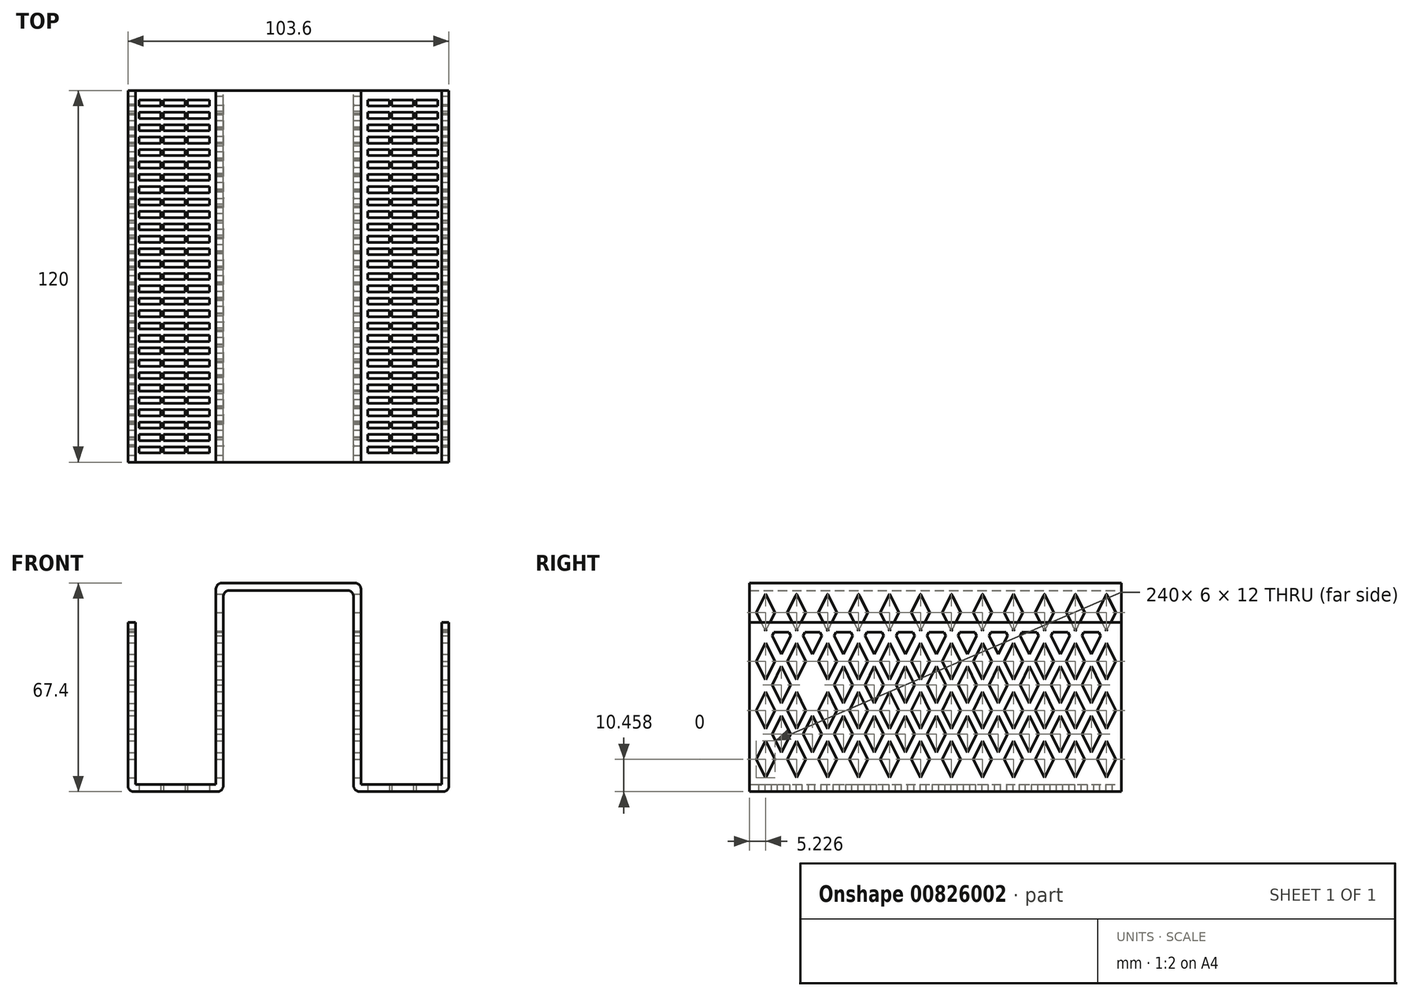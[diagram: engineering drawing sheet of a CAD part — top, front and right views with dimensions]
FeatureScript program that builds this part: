
annotation { "Feature Type Name" : "Feature", "Feature Type Description" : "" }
export const myFeature = defineFeature(function(context is Context, id is Id, definition is map)
    precondition{}
    {
        {
            var Q0;
            Q0=qCreatedBy(makeId("Front.planeOp"),FACE);
            var sketch = newSketch(context, id + "F0", { "sketchPlane" : qUnion([Q0])});
            skLineSegment(sketch, "E0", {"start": v(0, 0) * mm, "end": v(0, 123.96) * mm, "construction": true});
            skLineSegment(sketch, "E1", {"start": v(0, 43.65) * mm, "end": v(-23.4, 43.65) * mm});
            skLineSegment(sketch, "E2", {"start": v(-23.4, 43.65) * mm, "end": v(-23.4, -21.35) * mm});
            skLineSegment(sketch, "E3", {"start": v(-23.4, -21.35) * mm, "end": v(-49.4, -21.35) * mm});
            skLineSegment(sketch, "E4", {"start": v(-49.4, -21.35) * mm, "end": v(-49.4, 28.65) * mm});
            skLineSegment(sketch, "E5.MirrorCS", {"start": v(0, 43.65) * mm, "end": v(23.4, 43.65) * mm});
            skLineSegment(sketch, "E6.MirrorCS", {"start": v(23.4, 43.65) * mm, "end": v(23.4, -21.35) * mm});
            skLineSegment(sketch, "E7.MirrorCS", {"start": v(23.4, -21.35) * mm, "end": v(49.4, -21.35) * mm});
            skLineSegment(sketch, "E8.MirrorCS", {"start": v(49.4, -21.35) * mm, "end": v(49.4, 28.65) * mm});
            skLineSegment(sketch, "E9.0", {"start": v(-51.8, -23.75) * mm, "end": v(-51.8, 28.65) * mm});
            skLineSegment(sketch, "E9.1", {"start": v(-21, -23.75) * mm, "end": v(-51.8, -23.75) * mm});
            skLineSegment(sketch, "E9.2", {"start": v(-21, 41.25) * mm, "end": v(-21, -23.75) * mm});
            skLineSegment(sketch, "E9.3", {"start": v(0, 41.25) * mm, "end": v(-21, 41.25) * mm});
            skLineSegment(sketch, "E9.4", {"start": v(51.8, -23.75) * mm, "end": v(51.8, 28.65) * mm});
            skLineSegment(sketch, "E9.5", {"start": v(21, -23.75) * mm, "end": v(51.8, -23.75) * mm});
            skLineSegment(sketch, "E9.6", {"start": v(21, 41.25) * mm, "end": v(21, -23.75) * mm});
            skLineSegment(sketch, "E9.7", {"start": v(0, 41.25) * mm, "end": v(21, 41.25) * mm});
            skLineSegment(sketch, "E10", {"start": v(-51.8, 28.65) * mm, "end": v(-49.4, 28.65) * mm});
            skLineSegment(sketch, "E11", {"start": v(51.8, 28.65) * mm, "end": v(49.4, 28.65) * mm});
            skSolve(sketch);
        }
        {
            var Q0;
            Q0=makeQuery(id+"F0.imprint","IMPRINT",FACE,{"disambiguationData":[TD([[makeQuery(id+"F0.imprint","IMPRINT",EDGE,{"derivedFrom":sQuery(id+"F0.wireOp",EDGE,"E1")}),1.0]])]});
            extrude(context, id + "F1", {"entities" : qUnion([Q0]), "depth" : 60 * mm, "offsetDistance" : 25 * mm, "hasSecondDirection" : true, "secondDirectionOppositeDirection" : true, "secondDirectionDepth" : 60 * mm});
        }
        {
            var Q0;
            Q0=makeQuery(id+"F1.opExtrude","SWEPT_FACE",FACE,{"disambiguationData":[OSD([sQuery(id+"F0.wireOp",EDGE,"E9.4")])]});
            var sketch = newSketch(context, id + "F2", { "sketchPlane" : qUnion([Q0])});
            skLineSegment(sketch, "E12", {"start": v(-54.77, 34.1) * mm, "end": v(-54.77, 40.1) * mm, "construction": true});
            skLineSegment(sketch, "E13", {"start": v(-54.77, 34.1) * mm, "end": v(-54.77, 28.1) * mm, "construction": true});
            skLineSegment(sketch, "E14", {"start": v(-54.77, 34.1) * mm, "end": v(-51.77, 34.1) * mm, "construction": true});
            skLineSegment(sketch, "E15", {"start": v(-54.77, 34.1) * mm, "end": v(-57.77, 34.1) * mm, "construction": true});
            skLineSegment(sketch, "E16", {"start": v(-54.77, 40.1) * mm, "end": v(-51.77, 34.1) * mm});
            skLineSegment(sketch, "E17", {"start": v(-54.77, 28.1) * mm, "end": v(-51.77, 34.1) * mm});
            skLineSegment(sketch, "E18", {"start": v(-54.77, 28.1) * mm, "end": v(-57.77, 34.1) * mm});
            skLineSegment(sketch, "E19", {"start": v(-57.77, 34.1) * mm, "end": v(-54.77, 40.1) * mm});
            skLineSegment(sketch, "E20.0.1.0", {"start": v(-54.77, 24.3) * mm, "end": v(-51.77, 18.3) * mm});
            skLineSegment(sketch, "E20.0.1.1", {"start": v(-57.77, 18.3) * mm, "end": v(-54.77, 24.3) * mm});
            skLineSegment(sketch, "E20.0.1.2", {"start": v(-54.77, 12.3) * mm, "end": v(-57.77, 18.3) * mm});
            skLineSegment(sketch, "E20.0.1.3", {"start": v(-54.77, 12.3) * mm, "end": v(-51.77, 18.3) * mm});
            skLineSegment(sketch, "E20.0.2.0", {"start": v(-54.77, 8.5) * mm, "end": v(-51.77, 2.5) * mm});
            skLineSegment(sketch, "E20.0.2.1", {"start": v(-57.77, 2.5) * mm, "end": v(-54.77, 8.5) * mm});
            skLineSegment(sketch, "E20.0.2.2", {"start": v(-54.77, -3.5) * mm, "end": v(-57.77, 2.5) * mm});
            skLineSegment(sketch, "E20.0.2.3", {"start": v(-54.77, -3.5) * mm, "end": v(-51.77, 2.5) * mm});
            skLineSegment(sketch, "E20.0.3.0", {"start": v(-54.77, -7.3) * mm, "end": v(-51.77, -13.3) * mm});
            skLineSegment(sketch, "E20.0.3.1", {"start": v(-57.77, -13.3) * mm, "end": v(-54.77, -7.3) * mm});
            skLineSegment(sketch, "E20.0.3.2", {"start": v(-54.77, -19.3) * mm, "end": v(-57.77, -13.3) * mm});
            skLineSegment(sketch, "E20.0.3.3", {"start": v(-54.77, -19.3) * mm, "end": v(-51.77, -13.3) * mm});
            skLineSegment(sketch, "E20.1.0.0", {"start": v(-44.77, 40.1) * mm, "end": v(-41.77, 34.1) * mm});
            skLineSegment(sketch, "E20.1.0.1", {"start": v(-47.77, 34.1) * mm, "end": v(-44.77, 40.1) * mm});
            skLineSegment(sketch, "E20.1.0.2", {"start": v(-44.77, 28.1) * mm, "end": v(-47.77, 34.1) * mm});
            skLineSegment(sketch, "E20.1.0.3", {"start": v(-44.77, 28.1) * mm, "end": v(-41.77, 34.1) * mm});
            skLineSegment(sketch, "E20.1.1.0", {"start": v(-44.77, 24.3) * mm, "end": v(-41.77, 18.3) * mm});
            skLineSegment(sketch, "E20.1.1.1", {"start": v(-47.77, 18.3) * mm, "end": v(-44.77, 24.3) * mm});
            skLineSegment(sketch, "E20.1.1.2", {"start": v(-44.77, 12.3) * mm, "end": v(-47.77, 18.3) * mm});
            skLineSegment(sketch, "E20.1.1.3", {"start": v(-44.77, 12.3) * mm, "end": v(-41.77, 18.3) * mm});
            skLineSegment(sketch, "E20.1.2.0", {"start": v(-44.77, 8.5) * mm, "end": v(-41.77, 2.5) * mm});
            skLineSegment(sketch, "E20.1.2.1", {"start": v(-47.77, 2.5) * mm, "end": v(-44.77, 8.5) * mm});
            skLineSegment(sketch, "E20.1.2.2", {"start": v(-44.77, -3.5) * mm, "end": v(-47.77, 2.5) * mm});
            skLineSegment(sketch, "E20.1.2.3", {"start": v(-44.77, -3.5) * mm, "end": v(-41.77, 2.5) * mm});
            skLineSegment(sketch, "E20.1.3.0", {"start": v(-44.77, -7.3) * mm, "end": v(-41.77, -13.3) * mm});
            skLineSegment(sketch, "E20.1.3.1", {"start": v(-47.77, -13.3) * mm, "end": v(-44.77, -7.3) * mm});
            skLineSegment(sketch, "E20.1.3.2", {"start": v(-44.77, -19.3) * mm, "end": v(-47.77, -13.3) * mm});
            skLineSegment(sketch, "E20.1.3.3", {"start": v(-44.77, -19.3) * mm, "end": v(-41.77, -13.3) * mm});
            skLineSegment(sketch, "E20.2.0.0", {"start": v(-34.77, 40.1) * mm, "end": v(-31.77, 34.1) * mm});
            skLineSegment(sketch, "E20.2.0.1", {"start": v(-37.77, 34.1) * mm, "end": v(-34.77, 40.1) * mm});
            skLineSegment(sketch, "E20.2.0.2", {"start": v(-34.77, 28.1) * mm, "end": v(-37.77, 34.1) * mm});
            skLineSegment(sketch, "E20.2.0.3", {"start": v(-34.77, 28.1) * mm, "end": v(-31.77, 34.1) * mm});
            skLineSegment(sketch, "E20.2.1.0", {"start": v(-34.77, 24.3) * mm, "end": v(-31.77, 18.3) * mm});
            skLineSegment(sketch, "E20.2.1.1", {"start": v(-37.77, 18.3) * mm, "end": v(-34.77, 24.3) * mm});
            skLineSegment(sketch, "E20.2.1.2", {"start": v(-34.77, 12.3) * mm, "end": v(-37.77, 18.3) * mm});
            skLineSegment(sketch, "E20.2.1.3", {"start": v(-34.77, 12.3) * mm, "end": v(-31.77, 18.3) * mm});
            skLineSegment(sketch, "E20.2.2.0", {"start": v(-34.77, 8.5) * mm, "end": v(-31.77, 2.5) * mm});
            skLineSegment(sketch, "E20.2.2.1", {"start": v(-37.77, 2.5) * mm, "end": v(-34.77, 8.5) * mm});
            skLineSegment(sketch, "E20.2.2.2", {"start": v(-34.77, -3.5) * mm, "end": v(-37.77, 2.5) * mm});
            skLineSegment(sketch, "E20.2.2.3", {"start": v(-34.77, -3.5) * mm, "end": v(-31.77, 2.5) * mm});
            skLineSegment(sketch, "E20.2.3.0", {"start": v(-34.77, -7.3) * mm, "end": v(-31.77, -13.3) * mm});
            skLineSegment(sketch, "E20.2.3.1", {"start": v(-37.77, -13.3) * mm, "end": v(-34.77, -7.3) * mm});
            skLineSegment(sketch, "E20.2.3.2", {"start": v(-34.77, -19.3) * mm, "end": v(-37.77, -13.3) * mm});
            skLineSegment(sketch, "E20.2.3.3", {"start": v(-34.77, -19.3) * mm, "end": v(-31.77, -13.3) * mm});
            skLineSegment(sketch, "E20.3.0.0", {"start": v(-24.77, 40.1) * mm, "end": v(-21.77, 34.1) * mm});
            skLineSegment(sketch, "E20.3.0.1", {"start": v(-27.77, 34.1) * mm, "end": v(-24.77, 40.1) * mm});
            skLineSegment(sketch, "E20.3.0.2", {"start": v(-24.77, 28.1) * mm, "end": v(-27.77, 34.1) * mm});
            skLineSegment(sketch, "E20.3.0.3", {"start": v(-24.77, 28.1) * mm, "end": v(-21.77, 34.1) * mm});
            skLineSegment(sketch, "E20.3.1.0", {"start": v(-24.77, 24.3) * mm, "end": v(-21.77, 18.3) * mm});
            skLineSegment(sketch, "E20.3.1.1", {"start": v(-27.77, 18.3) * mm, "end": v(-24.77, 24.3) * mm});
            skLineSegment(sketch, "E20.3.1.2", {"start": v(-24.77, 12.3) * mm, "end": v(-27.77, 18.3) * mm});
            skLineSegment(sketch, "E20.3.1.3", {"start": v(-24.77, 12.3) * mm, "end": v(-21.77, 18.3) * mm});
            skLineSegment(sketch, "E20.3.2.0", {"start": v(-24.77, 8.5) * mm, "end": v(-21.77, 2.5) * mm});
            skLineSegment(sketch, "E20.3.2.1", {"start": v(-27.77, 2.5) * mm, "end": v(-24.77, 8.5) * mm});
            skLineSegment(sketch, "E20.3.2.2", {"start": v(-24.77, -3.5) * mm, "end": v(-27.77, 2.5) * mm});
            skLineSegment(sketch, "E20.3.2.3", {"start": v(-24.77, -3.5) * mm, "end": v(-21.77, 2.5) * mm});
            skLineSegment(sketch, "E20.3.3.0", {"start": v(-24.77, -7.3) * mm, "end": v(-21.77, -13.3) * mm});
            skLineSegment(sketch, "E20.3.3.1", {"start": v(-27.77, -13.3) * mm, "end": v(-24.77, -7.3) * mm});
            skLineSegment(sketch, "E20.3.3.2", {"start": v(-24.77, -19.3) * mm, "end": v(-27.77, -13.3) * mm});
            skLineSegment(sketch, "E20.3.3.3", {"start": v(-24.77, -19.3) * mm, "end": v(-21.77, -13.3) * mm});
            skLineSegment(sketch, "E20.4.0.0", {"start": v(-14.77, 40.1) * mm, "end": v(-11.77, 34.1) * mm});
            skLineSegment(sketch, "E20.4.0.1", {"start": v(-17.77, 34.1) * mm, "end": v(-14.77, 40.1) * mm});
            skLineSegment(sketch, "E20.4.0.2", {"start": v(-14.77, 28.1) * mm, "end": v(-17.77, 34.1) * mm});
            skLineSegment(sketch, "E20.4.0.3", {"start": v(-14.77, 28.1) * mm, "end": v(-11.77, 34.1) * mm});
            skLineSegment(sketch, "E20.4.1.0", {"start": v(-14.77, 24.3) * mm, "end": v(-11.77, 18.3) * mm});
            skLineSegment(sketch, "E20.4.1.1", {"start": v(-17.77, 18.3) * mm, "end": v(-14.77, 24.3) * mm});
            skLineSegment(sketch, "E20.4.1.2", {"start": v(-14.77, 12.3) * mm, "end": v(-17.77, 18.3) * mm});
            skLineSegment(sketch, "E20.4.1.3", {"start": v(-14.77, 12.3) * mm, "end": v(-11.77, 18.3) * mm});
            skLineSegment(sketch, "E20.4.2.0", {"start": v(-14.77, 8.5) * mm, "end": v(-11.77, 2.5) * mm});
            skLineSegment(sketch, "E20.4.2.1", {"start": v(-17.77, 2.5) * mm, "end": v(-14.77, 8.5) * mm});
            skLineSegment(sketch, "E20.4.2.2", {"start": v(-14.77, -3.5) * mm, "end": v(-17.77, 2.5) * mm});
            skLineSegment(sketch, "E20.4.2.3", {"start": v(-14.77, -3.5) * mm, "end": v(-11.77, 2.5) * mm});
            skLineSegment(sketch, "E20.4.3.0", {"start": v(-14.77, -7.3) * mm, "end": v(-11.77, -13.3) * mm});
            skLineSegment(sketch, "E20.4.3.1", {"start": v(-17.77, -13.3) * mm, "end": v(-14.77, -7.3) * mm});
            skLineSegment(sketch, "E20.4.3.2", {"start": v(-14.77, -19.3) * mm, "end": v(-17.77, -13.3) * mm});
            skLineSegment(sketch, "E20.4.3.3", {"start": v(-14.77, -19.3) * mm, "end": v(-11.77, -13.3) * mm});
            skLineSegment(sketch, "E20.5.0.0", {"start": v(-4.77, 40.1) * mm, "end": v(-1.77, 34.1) * mm});
            skLineSegment(sketch, "E20.5.0.1", {"start": v(-7.77, 34.1) * mm, "end": v(-4.77, 40.1) * mm});
            skLineSegment(sketch, "E20.5.0.2", {"start": v(-4.77, 28.1) * mm, "end": v(-7.77, 34.1) * mm});
            skLineSegment(sketch, "E20.5.0.3", {"start": v(-4.77, 28.1) * mm, "end": v(-1.77, 34.1) * mm});
            skLineSegment(sketch, "E20.5.1.0", {"start": v(-4.77, 24.3) * mm, "end": v(-1.77, 18.3) * mm});
            skLineSegment(sketch, "E20.5.1.1", {"start": v(-7.77, 18.3) * mm, "end": v(-4.77, 24.3) * mm});
            skLineSegment(sketch, "E20.5.1.2", {"start": v(-4.77, 12.3) * mm, "end": v(-7.77, 18.3) * mm});
            skLineSegment(sketch, "E20.5.1.3", {"start": v(-4.77, 12.3) * mm, "end": v(-1.77, 18.3) * mm});
            skLineSegment(sketch, "E20.5.2.0", {"start": v(-4.77, 8.5) * mm, "end": v(-1.77, 2.5) * mm});
            skLineSegment(sketch, "E20.5.2.1", {"start": v(-7.77, 2.5) * mm, "end": v(-4.77, 8.5) * mm});
            skLineSegment(sketch, "E20.5.2.2", {"start": v(-4.77, -3.5) * mm, "end": v(-7.77, 2.5) * mm});
            skLineSegment(sketch, "E20.5.2.3", {"start": v(-4.77, -3.5) * mm, "end": v(-1.77, 2.5) * mm});
            skLineSegment(sketch, "E20.5.3.0", {"start": v(-4.77, -7.3) * mm, "end": v(-1.77, -13.3) * mm});
            skLineSegment(sketch, "E20.5.3.1", {"start": v(-7.77, -13.3) * mm, "end": v(-4.77, -7.3) * mm});
            skLineSegment(sketch, "E20.5.3.2", {"start": v(-4.77, -19.3) * mm, "end": v(-7.77, -13.3) * mm});
            skLineSegment(sketch, "E20.5.3.3", {"start": v(-4.77, -19.3) * mm, "end": v(-1.77, -13.3) * mm});
            skLineSegment(sketch, "E20.6.0.0", {"start": v(5.23, 40.1) * mm, "end": v(8.23, 34.1) * mm});
            skLineSegment(sketch, "E20.6.0.1", {"start": v(2.23, 34.1) * mm, "end": v(5.23, 40.1) * mm});
            skLineSegment(sketch, "E20.6.0.2", {"start": v(5.23, 28.1) * mm, "end": v(2.23, 34.1) * mm});
            skLineSegment(sketch, "E20.6.0.3", {"start": v(5.23, 28.1) * mm, "end": v(8.23, 34.1) * mm});
            skLineSegment(sketch, "E20.6.1.0", {"start": v(5.23, 24.3) * mm, "end": v(8.23, 18.3) * mm});
            skLineSegment(sketch, "E20.6.1.1", {"start": v(2.23, 18.3) * mm, "end": v(5.23, 24.3) * mm});
            skLineSegment(sketch, "E20.6.1.2", {"start": v(5.23, 12.3) * mm, "end": v(2.23, 18.3) * mm});
            skLineSegment(sketch, "E20.6.1.3", {"start": v(5.23, 12.3) * mm, "end": v(8.23, 18.3) * mm});
            skLineSegment(sketch, "E20.6.2.0", {"start": v(5.23, 8.5) * mm, "end": v(8.23, 2.5) * mm});
            skLineSegment(sketch, "E20.6.2.1", {"start": v(2.23, 2.5) * mm, "end": v(5.23, 8.5) * mm});
            skLineSegment(sketch, "E20.6.2.2", {"start": v(5.23, -3.5) * mm, "end": v(2.23, 2.5) * mm});
            skLineSegment(sketch, "E20.6.2.3", {"start": v(5.23, -3.5) * mm, "end": v(8.23, 2.5) * mm});
            skLineSegment(sketch, "E20.6.3.0", {"start": v(5.23, -7.3) * mm, "end": v(8.23, -13.3) * mm});
            skLineSegment(sketch, "E20.6.3.1", {"start": v(2.23, -13.3) * mm, "end": v(5.23, -7.3) * mm});
            skLineSegment(sketch, "E20.6.3.2", {"start": v(5.23, -19.3) * mm, "end": v(2.23, -13.3) * mm});
            skLineSegment(sketch, "E20.6.3.3", {"start": v(5.23, -19.3) * mm, "end": v(8.23, -13.3) * mm});
            skLineSegment(sketch, "E20.7.0.0", {"start": v(15.23, 40.1) * mm, "end": v(18.23, 34.1) * mm});
            skLineSegment(sketch, "E20.7.0.1", {"start": v(12.23, 34.1) * mm, "end": v(15.23, 40.1) * mm});
            skLineSegment(sketch, "E20.7.0.2", {"start": v(15.23, 28.1) * mm, "end": v(12.23, 34.1) * mm});
            skLineSegment(sketch, "E20.7.0.3", {"start": v(15.23, 28.1) * mm, "end": v(18.23, 34.1) * mm});
            skLineSegment(sketch, "E20.7.1.0", {"start": v(15.23, 24.3) * mm, "end": v(18.23, 18.3) * mm});
            skLineSegment(sketch, "E20.7.1.1", {"start": v(12.23, 18.3) * mm, "end": v(15.23, 24.3) * mm});
            skLineSegment(sketch, "E20.7.1.2", {"start": v(15.23, 12.3) * mm, "end": v(12.23, 18.3) * mm});
            skLineSegment(sketch, "E20.7.1.3", {"start": v(15.23, 12.3) * mm, "end": v(18.23, 18.3) * mm});
            skLineSegment(sketch, "E20.7.2.0", {"start": v(15.23, 8.5) * mm, "end": v(18.23, 2.5) * mm});
            skLineSegment(sketch, "E20.7.2.1", {"start": v(12.23, 2.5) * mm, "end": v(15.23, 8.5) * mm});
            skLineSegment(sketch, "E20.7.2.2", {"start": v(15.23, -3.5) * mm, "end": v(12.23, 2.5) * mm});
            skLineSegment(sketch, "E20.7.2.3", {"start": v(15.23, -3.5) * mm, "end": v(18.23, 2.5) * mm});
            skLineSegment(sketch, "E20.7.3.0", {"start": v(15.23, -7.3) * mm, "end": v(18.23, -13.3) * mm});
            skLineSegment(sketch, "E20.7.3.1", {"start": v(12.23, -13.3) * mm, "end": v(15.23, -7.3) * mm});
            skLineSegment(sketch, "E20.7.3.2", {"start": v(15.23, -19.3) * mm, "end": v(12.23, -13.3) * mm});
            skLineSegment(sketch, "E20.7.3.3", {"start": v(15.23, -19.3) * mm, "end": v(18.23, -13.3) * mm});
            skLineSegment(sketch, "E20.8.0.0", {"start": v(25.23, 40.1) * mm, "end": v(28.23, 34.1) * mm});
            skLineSegment(sketch, "E20.8.0.1", {"start": v(22.23, 34.1) * mm, "end": v(25.23, 40.1) * mm});
            skLineSegment(sketch, "E20.8.0.2", {"start": v(25.23, 28.1) * mm, "end": v(22.23, 34.1) * mm});
            skLineSegment(sketch, "E20.8.0.3", {"start": v(25.23, 28.1) * mm, "end": v(28.23, 34.1) * mm});
            skLineSegment(sketch, "E20.8.1.0", {"start": v(25.23, 24.3) * mm, "end": v(28.23, 18.3) * mm});
            skLineSegment(sketch, "E20.8.1.1", {"start": v(22.23, 18.3) * mm, "end": v(25.23, 24.3) * mm});
            skLineSegment(sketch, "E20.8.1.2", {"start": v(25.23, 12.3) * mm, "end": v(22.23, 18.3) * mm});
            skLineSegment(sketch, "E20.8.1.3", {"start": v(25.23, 12.3) * mm, "end": v(28.23, 18.3) * mm});
            skLineSegment(sketch, "E20.8.2.0", {"start": v(25.23, 8.5) * mm, "end": v(28.23, 2.5) * mm});
            skLineSegment(sketch, "E20.8.2.1", {"start": v(22.23, 2.5) * mm, "end": v(25.23, 8.5) * mm});
            skLineSegment(sketch, "E20.8.2.2", {"start": v(25.23, -3.5) * mm, "end": v(22.23, 2.5) * mm});
            skLineSegment(sketch, "E20.8.2.3", {"start": v(25.23, -3.5) * mm, "end": v(28.23, 2.5) * mm});
            skLineSegment(sketch, "E20.8.3.0", {"start": v(25.23, -7.3) * mm, "end": v(28.23, -13.3) * mm});
            skLineSegment(sketch, "E20.8.3.1", {"start": v(22.23, -13.3) * mm, "end": v(25.23, -7.3) * mm});
            skLineSegment(sketch, "E20.8.3.2", {"start": v(25.23, -19.3) * mm, "end": v(22.23, -13.3) * mm});
            skLineSegment(sketch, "E20.8.3.3", {"start": v(25.23, -19.3) * mm, "end": v(28.23, -13.3) * mm});
            skLineSegment(sketch, "E20.9.0.0", {"start": v(35.23, 40.1) * mm, "end": v(38.23, 34.1) * mm});
            skLineSegment(sketch, "E20.9.0.1", {"start": v(32.23, 34.1) * mm, "end": v(35.23, 40.1) * mm});
            skLineSegment(sketch, "E20.9.0.2", {"start": v(35.23, 28.1) * mm, "end": v(32.23, 34.1) * mm});
            skLineSegment(sketch, "E20.9.0.3", {"start": v(35.23, 28.1) * mm, "end": v(38.23, 34.1) * mm});
            skLineSegment(sketch, "E20.9.1.0", {"start": v(35.23, 24.3) * mm, "end": v(38.23, 18.3) * mm});
            skLineSegment(sketch, "E20.9.1.1", {"start": v(32.23, 18.3) * mm, "end": v(35.23, 24.3) * mm});
            skLineSegment(sketch, "E20.9.1.2", {"start": v(35.23, 12.3) * mm, "end": v(32.23, 18.3) * mm});
            skLineSegment(sketch, "E20.9.1.3", {"start": v(35.23, 12.3) * mm, "end": v(38.23, 18.3) * mm});
            skLineSegment(sketch, "E20.9.2.0", {"start": v(35.23, 8.5) * mm, "end": v(38.23, 2.5) * mm});
            skLineSegment(sketch, "E20.9.2.1", {"start": v(32.23, 2.5) * mm, "end": v(35.23, 8.5) * mm});
            skLineSegment(sketch, "E20.9.2.2", {"start": v(35.23, -3.5) * mm, "end": v(32.23, 2.5) * mm});
            skLineSegment(sketch, "E20.9.2.3", {"start": v(35.23, -3.5) * mm, "end": v(38.23, 2.5) * mm});
            skLineSegment(sketch, "E20.9.3.0", {"start": v(35.23, -7.3) * mm, "end": v(38.23, -13.3) * mm});
            skLineSegment(sketch, "E20.9.3.1", {"start": v(32.23, -13.3) * mm, "end": v(35.23, -7.3) * mm});
            skLineSegment(sketch, "E20.9.3.2", {"start": v(35.23, -19.3) * mm, "end": v(32.23, -13.3) * mm});
            skLineSegment(sketch, "E20.9.3.3", {"start": v(35.23, -19.3) * mm, "end": v(38.23, -13.3) * mm});
            skLineSegment(sketch, "E20.10.0.0", {"start": v(45.23, 40.1) * mm, "end": v(48.23, 34.1) * mm});
            skLineSegment(sketch, "E20.10.0.1", {"start": v(42.23, 34.1) * mm, "end": v(45.23, 40.1) * mm});
            skLineSegment(sketch, "E20.10.0.2", {"start": v(45.23, 28.1) * mm, "end": v(42.23, 34.1) * mm});
            skLineSegment(sketch, "E20.10.0.3", {"start": v(45.23, 28.1) * mm, "end": v(48.23, 34.1) * mm});
            skLineSegment(sketch, "E20.10.1.0", {"start": v(45.23, 24.3) * mm, "end": v(48.23, 18.3) * mm});
            skLineSegment(sketch, "E20.10.1.1", {"start": v(42.23, 18.3) * mm, "end": v(45.23, 24.3) * mm});
            skLineSegment(sketch, "E20.10.1.2", {"start": v(45.23, 12.3) * mm, "end": v(42.23, 18.3) * mm});
            skLineSegment(sketch, "E20.10.1.3", {"start": v(45.23, 12.3) * mm, "end": v(48.23, 18.3) * mm});
            skLineSegment(sketch, "E20.10.2.0", {"start": v(45.23, 8.5) * mm, "end": v(48.23, 2.5) * mm});
            skLineSegment(sketch, "E20.10.2.1", {"start": v(42.23, 2.5) * mm, "end": v(45.23, 8.5) * mm});
            skLineSegment(sketch, "E20.10.2.2", {"start": v(45.23, -3.5) * mm, "end": v(42.23, 2.5) * mm});
            skLineSegment(sketch, "E20.10.2.3", {"start": v(45.23, -3.5) * mm, "end": v(48.23, 2.5) * mm});
            skLineSegment(sketch, "E20.10.3.0", {"start": v(45.23, -7.3) * mm, "end": v(48.23, -13.3) * mm});
            skLineSegment(sketch, "E20.10.3.1", {"start": v(42.23, -13.3) * mm, "end": v(45.23, -7.3) * mm});
            skLineSegment(sketch, "E20.10.3.2", {"start": v(45.23, -19.3) * mm, "end": v(42.23, -13.3) * mm});
            skLineSegment(sketch, "E20.10.3.3", {"start": v(45.23, -19.3) * mm, "end": v(48.23, -13.3) * mm});
            skLineSegment(sketch, "E20.11.0.0", {"start": v(55.23, 40.1) * mm, "end": v(58.23, 34.1) * mm});
            skLineSegment(sketch, "E20.11.0.1", {"start": v(52.23, 34.1) * mm, "end": v(55.23, 40.1) * mm});
            skLineSegment(sketch, "E20.11.0.2", {"start": v(55.23, 28.1) * mm, "end": v(52.23, 34.1) * mm});
            skLineSegment(sketch, "E20.11.0.3", {"start": v(55.23, 28.1) * mm, "end": v(58.23, 34.1) * mm});
            skLineSegment(sketch, "E20.11.1.0", {"start": v(55.23, 24.3) * mm, "end": v(58.23, 18.3) * mm});
            skLineSegment(sketch, "E20.11.1.1", {"start": v(52.23, 18.3) * mm, "end": v(55.23, 24.3) * mm});
            skLineSegment(sketch, "E20.11.1.2", {"start": v(55.23, 12.3) * mm, "end": v(52.23, 18.3) * mm});
            skLineSegment(sketch, "E20.11.1.3", {"start": v(55.23, 12.3) * mm, "end": v(58.23, 18.3) * mm});
            skLineSegment(sketch, "E20.11.2.0", {"start": v(55.23, 8.5) * mm, "end": v(58.23, 2.5) * mm});
            skLineSegment(sketch, "E20.11.2.1", {"start": v(52.23, 2.5) * mm, "end": v(55.23, 8.5) * mm});
            skLineSegment(sketch, "E20.11.2.2", {"start": v(55.23, -3.5) * mm, "end": v(52.23, 2.5) * mm});
            skLineSegment(sketch, "E20.11.2.3", {"start": v(55.23, -3.5) * mm, "end": v(58.23, 2.5) * mm});
            skLineSegment(sketch, "E20.11.3.0", {"start": v(55.23, -7.3) * mm, "end": v(58.23, -13.3) * mm});
            skLineSegment(sketch, "E20.11.3.1", {"start": v(52.23, -13.3) * mm, "end": v(55.23, -7.3) * mm});
            skLineSegment(sketch, "E20.11.3.2", {"start": v(55.23, -19.3) * mm, "end": v(52.23, -13.3) * mm});
            skLineSegment(sketch, "E20.11.3.3", {"start": v(55.23, -19.3) * mm, "end": v(58.23, -13.3) * mm});
            skLineSegment(sketch, "E20.direction1", {"start": v(-51.77, 34.1) * mm, "end": v(-41.77, 34.1) * mm, "construction": true});
            skLineSegment(sketch, "E20.direction2", {"start": v(-51.77, 34.1) * mm, "end": v(-51.77, 18.3) * mm, "construction": true});
            skLineSegment(sketch, "E21", {"start": v(-47.23, 27.78) * mm, "end": v(-46.67, 26.65) * mm});
            skLineSegment(sketch, "E22", {"start": v(-49.67, 20.65) * mm, "end": v(-46.67, 26.65) * mm});
            skLineSegment(sketch, "E23", {"start": v(-49.67, 20.65) * mm, "end": v(-52.67, 26.65) * mm});
            skLineSegment(sketch, "E24", {"start": v(-52.67, 26.65) * mm, "end": v(-52.1, 27.78) * mm});
            skLineSegment(sketch, "E25.0.1.0", {"start": v(-49.67, 16.75) * mm, "end": v(-46.67, 10.75) * mm});
            skLineSegment(sketch, "E25.0.1.1", {"start": v(-52.67, 10.75) * mm, "end": v(-49.67, 16.75) * mm});
            skLineSegment(sketch, "E25.0.1.2", {"start": v(-49.67, 4.75) * mm, "end": v(-52.67, 10.75) * mm});
            skLineSegment(sketch, "E25.0.1.3", {"start": v(-49.67, 4.75) * mm, "end": v(-46.67, 10.75) * mm});
            skLineSegment(sketch, "E25.0.2.0", {"start": v(-49.67, 0.85) * mm, "end": v(-46.67, -5.15) * mm});
            skLineSegment(sketch, "E25.0.2.1", {"start": v(-52.67, -5.15) * mm, "end": v(-49.67, 0.85) * mm});
            skLineSegment(sketch, "E25.0.2.2", {"start": v(-49.67, -11.15) * mm, "end": v(-52.67, -5.15) * mm});
            skLineSegment(sketch, "E25.0.2.3", {"start": v(-49.67, -11.15) * mm, "end": v(-46.67, -5.15) * mm});
            skLineSegment(sketch, "E25.1.1.1", {"start": v(-42.67, 10.75) * mm, "end": v(-39.67, 16.75) * mm});
            skLineSegment(sketch, "E25.1.1.2", {"start": v(-39.67, 4.75) * mm, "end": v(-42.67, 10.75) * mm});
            skLineSegment(sketch, "E25.1.1.3", {"start": v(-39.67, 4.75) * mm, "end": v(-36.67, 10.75) * mm});
            skLineSegment(sketch, "E25.1.2.0", {"start": v(-39.67, 0.85) * mm, "end": v(-36.67, -5.15) * mm});
            skLineSegment(sketch, "E25.1.2.1", {"start": v(-42.67, -5.15) * mm, "end": v(-39.67, 0.85) * mm});
            skLineSegment(sketch, "E25.1.2.2", {"start": v(-39.67, -11.15) * mm, "end": v(-42.67, -5.15) * mm});
            skLineSegment(sketch, "E25.1.2.3", {"start": v(-39.67, -11.15) * mm, "end": v(-36.67, -5.15) * mm});
            skLineSegment(sketch, "E25.2.1.0", {"start": v(-29.67, 16.75) * mm, "end": v(-26.67, 10.75) * mm});
            skLineSegment(sketch, "E25.2.1.1", {"start": v(-32.67, 10.75) * mm, "end": v(-29.67, 16.75) * mm});
            skLineSegment(sketch, "E25.2.1.2", {"start": v(-29.67, 4.75) * mm, "end": v(-32.67, 10.75) * mm});
            skLineSegment(sketch, "E25.2.1.3", {"start": v(-29.67, 4.75) * mm, "end": v(-26.67, 10.75) * mm});
            skLineSegment(sketch, "E25.2.2.0", {"start": v(-29.67, 0.85) * mm, "end": v(-26.67, -5.15) * mm});
            skLineSegment(sketch, "E25.2.2.1", {"start": v(-32.67, -5.15) * mm, "end": v(-29.67, 0.85) * mm});
            skLineSegment(sketch, "E25.2.2.2", {"start": v(-29.67, -11.15) * mm, "end": v(-32.67, -5.15) * mm});
            skLineSegment(sketch, "E25.2.2.3", {"start": v(-29.67, -11.15) * mm, "end": v(-26.67, -5.15) * mm});
            skLineSegment(sketch, "E25.3.1.1", {"start": v(-22.67, 10.75) * mm, "end": v(-19.67, 16.75) * mm});
            skLineSegment(sketch, "E25.3.1.2", {"start": v(-19.67, 4.75) * mm, "end": v(-22.67, 10.75) * mm});
            skLineSegment(sketch, "E25.3.1.3", {"start": v(-19.67, 4.75) * mm, "end": v(-16.67, 10.75) * mm});
            skLineSegment(sketch, "E25.3.2.0", {"start": v(-19.67, 0.85) * mm, "end": v(-16.67, -5.15) * mm});
            skLineSegment(sketch, "E25.3.2.1", {"start": v(-22.67, -5.15) * mm, "end": v(-19.67, 0.85) * mm});
            skLineSegment(sketch, "E25.3.2.2", {"start": v(-19.67, -11.15) * mm, "end": v(-22.67, -5.15) * mm});
            skLineSegment(sketch, "E25.3.2.3", {"start": v(-19.67, -11.15) * mm, "end": v(-16.67, -5.15) * mm});
            skLineSegment(sketch, "E25.4.1.0", {"start": v(-9.67, 16.75) * mm, "end": v(-6.67, 10.75) * mm});
            skLineSegment(sketch, "E25.4.1.1", {"start": v(-12.67, 10.75) * mm, "end": v(-9.67, 16.75) * mm});
            skLineSegment(sketch, "E25.4.1.2", {"start": v(-9.67, 4.75) * mm, "end": v(-12.67, 10.75) * mm});
            skLineSegment(sketch, "E25.4.1.3", {"start": v(-9.67, 4.75) * mm, "end": v(-6.67, 10.75) * mm});
            skLineSegment(sketch, "E25.4.2.0", {"start": v(-9.67, 0.85) * mm, "end": v(-6.67, -5.15) * mm});
            skLineSegment(sketch, "E25.4.2.1", {"start": v(-12.67, -5.15) * mm, "end": v(-9.67, 0.85) * mm});
            skLineSegment(sketch, "E25.4.2.2", {"start": v(-9.67, -11.15) * mm, "end": v(-12.67, -5.15) * mm});
            skLineSegment(sketch, "E25.4.2.3", {"start": v(-9.67, -11.15) * mm, "end": v(-6.67, -5.15) * mm});
            skLineSegment(sketch, "E25.5.1.0", {"start": v(0.33, 16.75) * mm, "end": v(3.33, 10.75) * mm});
            skLineSegment(sketch, "E25.5.1.1", {"start": v(-2.67, 10.75) * mm, "end": v(0.33, 16.75) * mm});
            skLineSegment(sketch, "E25.5.1.2", {"start": v(0.33, 4.75) * mm, "end": v(-2.67, 10.75) * mm});
            skLineSegment(sketch, "E25.5.1.3", {"start": v(0.33, 4.75) * mm, "end": v(3.33, 10.75) * mm});
            skLineSegment(sketch, "E25.5.2.0", {"start": v(0.33, 0.85) * mm, "end": v(3.33, -5.15) * mm});
            skLineSegment(sketch, "E25.5.2.1", {"start": v(-2.67, -5.15) * mm, "end": v(0.33, 0.85) * mm});
            skLineSegment(sketch, "E25.5.2.2", {"start": v(0.33, -11.15) * mm, "end": v(-2.67, -5.15) * mm});
            skLineSegment(sketch, "E25.5.2.3", {"start": v(0.33, -11.15) * mm, "end": v(3.33, -5.15) * mm});
            skLineSegment(sketch, "E25.6.1.0", {"start": v(10.33, 16.75) * mm, "end": v(13.33, 10.75) * mm});
            skLineSegment(sketch, "E25.6.1.1", {"start": v(7.33, 10.75) * mm, "end": v(10.33, 16.75) * mm});
            skLineSegment(sketch, "E25.6.1.2", {"start": v(10.33, 4.75) * mm, "end": v(7.33, 10.75) * mm});
            skLineSegment(sketch, "E25.6.1.3", {"start": v(10.33, 4.75) * mm, "end": v(13.33, 10.75) * mm});
            skLineSegment(sketch, "E25.6.2.0", {"start": v(10.33, 0.85) * mm, "end": v(13.33, -5.15) * mm});
            skLineSegment(sketch, "E25.6.2.1", {"start": v(7.33, -5.15) * mm, "end": v(10.33, 0.85) * mm});
            skLineSegment(sketch, "E25.6.2.2", {"start": v(10.33, -11.15) * mm, "end": v(7.33, -5.15) * mm});
            skLineSegment(sketch, "E25.6.2.3", {"start": v(10.33, -11.15) * mm, "end": v(13.33, -5.15) * mm});
            skLineSegment(sketch, "E25.7.1.0", {"start": v(20.33, 16.75) * mm, "end": v(23.33, 10.75) * mm});
            skLineSegment(sketch, "E25.7.1.1", {"start": v(17.33, 10.75) * mm, "end": v(20.33, 16.75) * mm});
            skLineSegment(sketch, "E25.7.1.2", {"start": v(20.33, 4.75) * mm, "end": v(17.33, 10.75) * mm});
            skLineSegment(sketch, "E25.7.1.3", {"start": v(20.33, 4.75) * mm, "end": v(23.33, 10.75) * mm});
            skLineSegment(sketch, "E25.7.2.0", {"start": v(20.33, 0.85) * mm, "end": v(23.33, -5.15) * mm});
            skLineSegment(sketch, "E25.7.2.1", {"start": v(17.33, -5.15) * mm, "end": v(20.33, 0.85) * mm});
            skLineSegment(sketch, "E25.7.2.2", {"start": v(20.33, -11.15) * mm, "end": v(17.33, -5.15) * mm});
            skLineSegment(sketch, "E25.7.2.3", {"start": v(20.33, -11.15) * mm, "end": v(23.33, -5.15) * mm});
            skLineSegment(sketch, "E25.8.1.0", {"start": v(30.33, 16.75) * mm, "end": v(33.33, 10.75) * mm});
            skLineSegment(sketch, "E25.8.1.1", {"start": v(27.33, 10.75) * mm, "end": v(30.33, 16.75) * mm});
            skLineSegment(sketch, "E25.8.1.2", {"start": v(30.33, 4.75) * mm, "end": v(27.33, 10.75) * mm});
            skLineSegment(sketch, "E25.8.1.3", {"start": v(30.33, 4.75) * mm, "end": v(33.33, 10.75) * mm});
            skLineSegment(sketch, "E25.8.2.0", {"start": v(30.33, 0.85) * mm, "end": v(33.33, -5.15) * mm});
            skLineSegment(sketch, "E25.8.2.1", {"start": v(27.33, -5.15) * mm, "end": v(30.33, 0.85) * mm});
            skLineSegment(sketch, "E25.8.2.2", {"start": v(30.33, -11.15) * mm, "end": v(27.33, -5.15) * mm});
            skLineSegment(sketch, "E25.8.2.3", {"start": v(30.33, -11.15) * mm, "end": v(33.33, -5.15) * mm});
            skLineSegment(sketch, "E25.9.1.0", {"start": v(40.33, 16.75) * mm, "end": v(43.33, 10.75) * mm});
            skLineSegment(sketch, "E25.9.1.1", {"start": v(37.33, 10.75) * mm, "end": v(40.33, 16.75) * mm});
            skLineSegment(sketch, "E25.9.1.2", {"start": v(40.33, 4.75) * mm, "end": v(37.33, 10.75) * mm});
            skLineSegment(sketch, "E25.9.1.3", {"start": v(40.33, 4.75) * mm, "end": v(43.33, 10.75) * mm});
            skLineSegment(sketch, "E25.9.2.0", {"start": v(40.33, 0.85) * mm, "end": v(43.33, -5.15) * mm});
            skLineSegment(sketch, "E25.9.2.1", {"start": v(37.33, -5.15) * mm, "end": v(40.33, 0.85) * mm});
            skLineSegment(sketch, "E25.9.2.2", {"start": v(40.33, -11.15) * mm, "end": v(37.33, -5.15) * mm});
            skLineSegment(sketch, "E25.9.2.3", {"start": v(40.33, -11.15) * mm, "end": v(43.33, -5.15) * mm});
            skLineSegment(sketch, "E25.10.1.0", {"start": v(50.33, 16.75) * mm, "end": v(53.33, 10.75) * mm});
            skLineSegment(sketch, "E25.10.1.1", {"start": v(47.33, 10.75) * mm, "end": v(50.33, 16.75) * mm});
            skLineSegment(sketch, "E25.10.1.2", {"start": v(50.33, 4.75) * mm, "end": v(47.33, 10.75) * mm});
            skLineSegment(sketch, "E25.10.1.3", {"start": v(50.33, 4.75) * mm, "end": v(53.33, 10.75) * mm});
            skLineSegment(sketch, "E25.10.2.0", {"start": v(50.33, 0.85) * mm, "end": v(53.33, -5.15) * mm});
            skLineSegment(sketch, "E25.10.2.1", {"start": v(47.33, -5.15) * mm, "end": v(50.33, 0.85) * mm});
            skLineSegment(sketch, "E25.10.2.2", {"start": v(50.33, -11.15) * mm, "end": v(47.33, -5.15) * mm});
            skLineSegment(sketch, "E25.10.2.3", {"start": v(50.33, -11.15) * mm, "end": v(53.33, -5.15) * mm});
            skLineSegment(sketch, "E25.direction1", {"start": v(-49.67, 20.65) * mm, "end": v(-39.67, 20.65) * mm, "construction": true});
            skLineSegment(sketch, "E25.direction2", {"start": v(-49.67, 20.65) * mm, "end": v(-49.67, 4.75) * mm, "construction": true});
            skLineSegment(sketch, "E26", {"start": v(-52.1, 27.78) * mm, "end": v(-47.23, 27.78) * mm});
            skPoint(sketch, "E27.orphan", {"position": v(-49.67, 32.65) * mm});
            skLineSegment(sketch, "E28.1.0.0", {"start": v(-42.1, 27.78) * mm, "end": v(-37.23, 27.78) * mm});
            skLineSegment(sketch, "E28.1.0.1", {"start": v(-37.23, 27.78) * mm, "end": v(-36.67, 26.65) * mm});
            skLineSegment(sketch, "E28.1.0.2", {"start": v(-39.67, 20.65) * mm, "end": v(-36.67, 26.65) * mm});
            skLineSegment(sketch, "E28.1.0.3", {"start": v(-39.67, 20.65) * mm, "end": v(-42.67, 26.65) * mm});
            skLineSegment(sketch, "E28.1.0.4", {"start": v(-42.67, 26.65) * mm, "end": v(-42.1, 27.78) * mm});
            skLineSegment(sketch, "E28.2.0.0", {"start": v(-32.1, 27.78) * mm, "end": v(-27.23, 27.78) * mm});
            skLineSegment(sketch, "E28.2.0.1", {"start": v(-27.23, 27.78) * mm, "end": v(-26.67, 26.65) * mm});
            skLineSegment(sketch, "E28.2.0.2", {"start": v(-29.67, 20.65) * mm, "end": v(-26.67, 26.65) * mm});
            skLineSegment(sketch, "E28.2.0.3", {"start": v(-29.67, 20.65) * mm, "end": v(-32.67, 26.65) * mm});
            skLineSegment(sketch, "E28.2.0.4", {"start": v(-32.67, 26.65) * mm, "end": v(-32.1, 27.78) * mm});
            skLineSegment(sketch, "E28.3.0.0", {"start": v(-22.1, 27.78) * mm, "end": v(-17.23, 27.78) * mm});
            skLineSegment(sketch, "E28.3.0.1", {"start": v(-17.23, 27.78) * mm, "end": v(-16.67, 26.65) * mm});
            skLineSegment(sketch, "E28.3.0.2", {"start": v(-19.67, 20.65) * mm, "end": v(-16.67, 26.65) * mm});
            skLineSegment(sketch, "E28.3.0.3", {"start": v(-19.67, 20.65) * mm, "end": v(-22.67, 26.65) * mm});
            skLineSegment(sketch, "E28.3.0.4", {"start": v(-22.67, 26.65) * mm, "end": v(-22.1, 27.78) * mm});
            skLineSegment(sketch, "E28.4.0.0", {"start": v(-12.1, 27.78) * mm, "end": v(-7.23, 27.78) * mm});
            skLineSegment(sketch, "E28.4.0.1", {"start": v(-7.23, 27.78) * mm, "end": v(-6.67, 26.65) * mm});
            skLineSegment(sketch, "E28.4.0.2", {"start": v(-9.67, 20.65) * mm, "end": v(-6.67, 26.65) * mm});
            skLineSegment(sketch, "E28.4.0.3", {"start": v(-9.67, 20.65) * mm, "end": v(-12.67, 26.65) * mm});
            skLineSegment(sketch, "E28.4.0.4", {"start": v(-12.67, 26.65) * mm, "end": v(-12.1, 27.78) * mm});
            skLineSegment(sketch, "E28.5.0.0", {"start": v(-2.1, 27.78) * mm, "end": v(2.77, 27.78) * mm});
            skLineSegment(sketch, "E28.5.0.1", {"start": v(2.77, 27.78) * mm, "end": v(3.33, 26.65) * mm});
            skLineSegment(sketch, "E28.5.0.2", {"start": v(0.33, 20.65) * mm, "end": v(3.33, 26.65) * mm});
            skLineSegment(sketch, "E28.5.0.3", {"start": v(0.33, 20.65) * mm, "end": v(-2.67, 26.65) * mm});
            skLineSegment(sketch, "E28.5.0.4", {"start": v(-2.67, 26.65) * mm, "end": v(-2.1, 27.78) * mm});
            skLineSegment(sketch, "E28.6.0.0", {"start": v(7.9, 27.78) * mm, "end": v(12.77, 27.78) * mm});
            skLineSegment(sketch, "E28.6.0.1", {"start": v(12.77, 27.78) * mm, "end": v(13.33, 26.65) * mm});
            skLineSegment(sketch, "E28.6.0.2", {"start": v(10.33, 20.65) * mm, "end": v(13.33, 26.65) * mm});
            skLineSegment(sketch, "E28.6.0.3", {"start": v(10.33, 20.65) * mm, "end": v(7.33, 26.65) * mm});
            skLineSegment(sketch, "E28.6.0.4", {"start": v(7.33, 26.65) * mm, "end": v(7.9, 27.78) * mm});
            skLineSegment(sketch, "E28.7.0.0", {"start": v(17.9, 27.78) * mm, "end": v(22.77, 27.78) * mm});
            skLineSegment(sketch, "E28.7.0.1", {"start": v(22.77, 27.78) * mm, "end": v(23.33, 26.65) * mm});
            skLineSegment(sketch, "E28.7.0.2", {"start": v(20.33, 20.65) * mm, "end": v(23.33, 26.65) * mm});
            skLineSegment(sketch, "E28.7.0.3", {"start": v(20.33, 20.65) * mm, "end": v(17.33, 26.65) * mm});
            skLineSegment(sketch, "E28.7.0.4", {"start": v(17.33, 26.65) * mm, "end": v(17.9, 27.78) * mm});
            skLineSegment(sketch, "E28.8.0.0", {"start": v(27.9, 27.78) * mm, "end": v(32.77, 27.78) * mm});
            skLineSegment(sketch, "E28.8.0.1", {"start": v(32.77, 27.78) * mm, "end": v(33.33, 26.65) * mm});
            skLineSegment(sketch, "E28.8.0.2", {"start": v(30.33, 20.65) * mm, "end": v(33.33, 26.65) * mm});
            skLineSegment(sketch, "E28.8.0.3", {"start": v(30.33, 20.65) * mm, "end": v(27.33, 26.65) * mm});
            skLineSegment(sketch, "E28.8.0.4", {"start": v(27.33, 26.65) * mm, "end": v(27.9, 27.78) * mm});
            skLineSegment(sketch, "E28.9.0.0", {"start": v(37.9, 27.78) * mm, "end": v(42.77, 27.78) * mm});
            skLineSegment(sketch, "E28.9.0.1", {"start": v(42.77, 27.78) * mm, "end": v(43.33, 26.65) * mm});
            skLineSegment(sketch, "E28.9.0.2", {"start": v(40.33, 20.65) * mm, "end": v(43.33, 26.65) * mm});
            skLineSegment(sketch, "E28.9.0.3", {"start": v(40.33, 20.65) * mm, "end": v(37.33, 26.65) * mm});
            skLineSegment(sketch, "E28.9.0.4", {"start": v(37.33, 26.65) * mm, "end": v(37.9, 27.78) * mm});
            skLineSegment(sketch, "E28.10.0.0", {"start": v(47.9, 27.78) * mm, "end": v(52.77, 27.78) * mm});
            skLineSegment(sketch, "E28.10.0.1", {"start": v(52.77, 27.78) * mm, "end": v(53.33, 26.65) * mm});
            skLineSegment(sketch, "E28.10.0.2", {"start": v(50.33, 20.65) * mm, "end": v(53.33, 26.65) * mm});
            skLineSegment(sketch, "E28.10.0.3", {"start": v(50.33, 20.65) * mm, "end": v(47.33, 26.65) * mm});
            skLineSegment(sketch, "E28.10.0.4", {"start": v(47.33, 26.65) * mm, "end": v(47.9, 27.78) * mm});
            skLineSegment(sketch, "E28.direction1", {"start": v(-52.1, 27.78) * mm, "end": v(-42.1, 27.78) * mm, "construction": true});
            skLineSegment(sketch, "E29", {"start": v(-19.67, 16.75) * mm, "end": v(-16.67, 10.75) * mm});
            skSolve(sketch);
        }
        {
            var Q0;
            Q0 = qSketchRegion(id + "F2", true);
            extrude(context, id + "F3", {"entities" : qUnion([Q0]), "operationType" : NewBodyOperationType.REMOVE, "oppositeDirection" : true, "depth" : 130 * mm, "offsetDistance" : 25 * mm});
        }
        {
            var Q0;
            Q0=makeQuery(id+"F1.opExtrude","CAP_FACE",FACE,{"disambiguationData":[OSD([sQuery(id+"F0.wireOp",EDGE,"E1"),sQuery(id+"F0.wireOp",EDGE,"E2"),sQuery(id+"F0.wireOp",EDGE,"E3"),sQuery(id+"F0.wireOp",EDGE,"E4"),sQuery(id+"F0.wireOp",EDGE,"E5.MirrorCS"),sQuery(id+"F0.wireOp",EDGE,"E6.MirrorCS"),sQuery(id+"F0.wireOp",EDGE,"E7.MirrorCS"),sQuery(id+"F0.wireOp",EDGE,"E8.MirrorCS"),sQuery(id+"F0.wireOp",EDGE,"E9.0"),sQuery(id+"F0.wireOp",EDGE,"E9.1"),sQuery(id+"F0.wireOp",EDGE,"E9.2"),sQuery(id+"F0.wireOp",EDGE,"E9.3"),sQuery(id+"F0.wireOp",EDGE,"E9.4"),sQuery(id+"F0.wireOp",EDGE,"E9.5"),sQuery(id+"F0.wireOp",EDGE,"E9.6"),sQuery(id+"F0.wireOp",EDGE,"E9.7"),sQuery(id+"F0.wireOp",EDGE,"E10"),sQuery(id+"F0.wireOp",EDGE,"E11")])],"isStart":false});
            var sketch = newSketch(context, id + "F4", { "sketchPlane" : qUnion([Q0])});
            skLineSegment(sketch, "E30.bottom", {"start": v(-49.4, 30.88) * mm, "end": v(-51.8, 30.88) * mm});
            skLineSegment(sketch, "E30.top", {"start": v(-49.4, 27.96) * mm, "end": v(-51.8, 27.96) * mm});
            skLineSegment(sketch, "E30.left", {"start": v(-49.4, 30.88) * mm, "end": v(-49.4, 27.96) * mm});
            skLineSegment(sketch, "E30.right", {"start": v(-51.8, 30.88) * mm, "end": v(-51.8, 27.96) * mm});
            skLineSegment(sketch, "E31", {"start": v(0, 0.79) * mm, "end": v(0, 10.47) * mm, "construction": true});
            skLineSegment(sketch, "E32.MirrorCS", {"start": v(49.4, 30.88) * mm, "end": v(49.4, 27.96) * mm});
            skLineSegment(sketch, "E33.MirrorCS", {"start": v(49.4, 30.88) * mm, "end": v(51.8, 30.88) * mm});
            skLineSegment(sketch, "E34.MirrorCS", {"start": v(51.8, 30.88) * mm, "end": v(51.8, 27.96) * mm});
            skLineSegment(sketch, "E35.MirrorCS", {"start": v(49.4, 27.96) * mm, "end": v(51.8, 27.96) * mm});
            skSolve(sketch);
        }
        {
            var Q0;
            {var subQ0=sQuery(id+"F4.wireOp",EDGE,"E30.bottom");Q0=makeQuery(id+"F4.imprint","IMPRINT",FACE,{"disambiguationData":[TD([[makeQuery(id+"F4.imprint","IMPRINT",EDGE,{"derivedFrom":subQ0}),1.0]])]});}
            var Q1;
            {var subQ2=sQuery(id+"F4.wireOp",EDGE,"E33.MirrorCS");Q1=makeQuery(id+"F4.imprint","IMPRINT",FACE,{"disambiguationData":[TD([[makeQuery(id+"F4.imprint","IMPRINT",EDGE,{"derivedFrom":subQ2}),-1.0]])]});}
            extrude(context, id + "F5", {"entities" : qUnion([Q0, Q1]), "operationType" : NewBodyOperationType.ADD, "oppositeDirection" : true, "depth" : 120 * mm, "offsetDistance" : 25 * mm});
        }
        {
            var Q0;
            Q0=makeQuery(id+"F1.opExtrude","SWEPT_EDGE",EDGE,{"disambiguationData":[OSD([sQuery(id+"F0.wireOp",EDGE,"E5.MirrorCS"),sQuery(id+"F0.wireOp",EDGE,"E6.MirrorCS")])]});
            var Q1;
            Q1=makeQuery(id+"F1.opExtrude","SWEPT_EDGE",EDGE,{"disambiguationData":[OSD([sQuery(id+"F0.wireOp",EDGE,"E1"),sQuery(id+"F0.wireOp",EDGE,"E2")])]});
            var Q2;
            Q2=makeQuery(id+"F1.opExtrude","SWEPT_EDGE",EDGE,{"disambiguationData":[OSD([sQuery(id+"F0.wireOp",EDGE,"E9.2"),sQuery(id+"F0.wireOp",EDGE,"E9.3")])]});
            var Q3;
            Q3=makeQuery(id+"F1.opExtrude","SWEPT_EDGE",EDGE,{"disambiguationData":[OSD([sQuery(id+"F0.wireOp",EDGE,"E9.6"),sQuery(id+"F0.wireOp",EDGE,"E9.7")])]});
            var Q4;
            Q4=makeQuery(id+"F1.opExtrude","SWEPT_EDGE",EDGE,{"disambiguationData":[OSD([sQuery(id+"F0.wireOp",EDGE,"E9.5"),sQuery(id+"F0.wireOp",EDGE,"E9.6")])]});
            var Q5;
            Q5=makeQuery(id+"F1.opExtrude","SWEPT_EDGE",EDGE,{"disambiguationData":[OSD([sQuery(id+"F0.wireOp",EDGE,"E9.0"),sQuery(id+"F0.wireOp",EDGE,"E9.1")])]});
            var Q6;
            Q6=makeQuery(id+"F1.opExtrude","SWEPT_EDGE",EDGE,{"disambiguationData":[OSD([sQuery(id+"F0.wireOp",EDGE,"E9.1"),sQuery(id+"F0.wireOp",EDGE,"E9.2")])]});
            var Q7;
            Q7=makeQuery(id+"F1.opExtrude","SWEPT_EDGE",EDGE,{"disambiguationData":[OSD([sQuery(id+"F0.wireOp",EDGE,"E9.4"),sQuery(id+"F0.wireOp",EDGE,"E9.5")])]});
            fillet(context, id + "F6", {"entities" : qUnion([Q0, Q1, Q2, Q3, Q4, Q5, Q6, Q7]), "radius" : 2 * mm, "tangentPropagation" : true, "allowEdgeOverflow" : false});
        }
        {
            var Q0;
            Q0=makeQuery(id+"F1.opExtrude","SWEPT_FACE",FACE,{"disambiguationData":[OSD([sQuery(id+"F0.wireOp",EDGE,"E9.1")])]});
            var sketch = newSketch(context, id + "F7", { "sketchPlane" : qUnion([Q0])});
            skLineSegment(sketch, "E36.bottom", {"start": v(-48.21, -56.95) * mm, "end": v(-41.21, -56.95) * mm});
            skLineSegment(sketch, "E36.top", {"start": v(-48.21, -54.95) * mm, "end": v(-41.21, -54.95) * mm});
            skLineSegment(sketch, "E36.left", {"start": v(-48.21, -56.95) * mm, "end": v(-48.21, -54.95) * mm});
            skLineSegment(sketch, "E36.right", {"start": v(-41.21, -56.95) * mm, "end": v(-41.21, -54.95) * mm});
            skLineSegment(sketch, "E37.0.1.0", {"start": v(-48.21, -50.95) * mm, "end": v(-41.21, -50.95) * mm});
            skLineSegment(sketch, "E37.0.1.1", {"start": v(-48.21, -52.95) * mm, "end": v(-41.21, -52.95) * mm});
            skLineSegment(sketch, "E37.0.1.2", {"start": v(-48.21, -52.95) * mm, "end": v(-48.21, -50.95) * mm});
            skLineSegment(sketch, "E37.0.1.3", {"start": v(-41.21, -52.95) * mm, "end": v(-41.21, -50.95) * mm});
            skLineSegment(sketch, "E37.0.2.0", {"start": v(-48.21, -46.95) * mm, "end": v(-41.21, -46.95) * mm});
            skLineSegment(sketch, "E37.0.2.1", {"start": v(-48.21, -48.95) * mm, "end": v(-41.21, -48.95) * mm});
            skLineSegment(sketch, "E37.0.2.2", {"start": v(-48.21, -48.95) * mm, "end": v(-48.21, -46.95) * mm});
            skLineSegment(sketch, "E37.0.2.3", {"start": v(-41.21, -48.95) * mm, "end": v(-41.21, -46.95) * mm});
            skLineSegment(sketch, "E37.0.3.0", {"start": v(-48.21, -42.95) * mm, "end": v(-41.21, -42.95) * mm});
            skLineSegment(sketch, "E37.0.3.1", {"start": v(-48.21, -44.95) * mm, "end": v(-41.21, -44.95) * mm});
            skLineSegment(sketch, "E37.0.3.2", {"start": v(-48.21, -44.95) * mm, "end": v(-48.21, -42.95) * mm});
            skLineSegment(sketch, "E37.0.3.3", {"start": v(-41.21, -44.95) * mm, "end": v(-41.21, -42.95) * mm});
            skLineSegment(sketch, "E37.0.4.0", {"start": v(-48.21, -38.95) * mm, "end": v(-41.21, -38.95) * mm});
            skLineSegment(sketch, "E37.0.4.1", {"start": v(-48.21, -40.95) * mm, "end": v(-41.21, -40.95) * mm});
            skLineSegment(sketch, "E37.0.4.2", {"start": v(-48.21, -40.95) * mm, "end": v(-48.21, -38.95) * mm});
            skLineSegment(sketch, "E37.0.4.3", {"start": v(-41.21, -40.95) * mm, "end": v(-41.21, -38.95) * mm});
            skLineSegment(sketch, "E37.0.5.0", {"start": v(-48.21, -34.95) * mm, "end": v(-41.21, -34.95) * mm});
            skLineSegment(sketch, "E37.0.5.1", {"start": v(-48.21, -36.95) * mm, "end": v(-41.21, -36.95) * mm});
            skLineSegment(sketch, "E37.0.5.2", {"start": v(-48.21, -36.95) * mm, "end": v(-48.21, -34.95) * mm});
            skLineSegment(sketch, "E37.0.5.3", {"start": v(-41.21, -36.95) * mm, "end": v(-41.21, -34.95) * mm});
            skLineSegment(sketch, "E37.0.6.0", {"start": v(-48.21, -30.95) * mm, "end": v(-41.21, -30.95) * mm});
            skLineSegment(sketch, "E37.0.6.1", {"start": v(-48.21, -32.95) * mm, "end": v(-41.21, -32.95) * mm});
            skLineSegment(sketch, "E37.0.6.2", {"start": v(-48.21, -32.95) * mm, "end": v(-48.21, -30.95) * mm});
            skLineSegment(sketch, "E37.0.6.3", {"start": v(-41.21, -32.95) * mm, "end": v(-41.21, -30.95) * mm});
            skLineSegment(sketch, "E37.0.7.0", {"start": v(-48.21, -26.95) * mm, "end": v(-41.21, -26.95) * mm});
            skLineSegment(sketch, "E37.0.7.1", {"start": v(-48.21, -28.95) * mm, "end": v(-41.21, -28.95) * mm});
            skLineSegment(sketch, "E37.0.7.2", {"start": v(-48.21, -28.95) * mm, "end": v(-48.21, -26.95) * mm});
            skLineSegment(sketch, "E37.0.7.3", {"start": v(-41.21, -28.95) * mm, "end": v(-41.21, -26.95) * mm});
            skLineSegment(sketch, "E37.0.8.0", {"start": v(-48.21, -22.95) * mm, "end": v(-41.21, -22.95) * mm});
            skLineSegment(sketch, "E37.0.8.1", {"start": v(-48.21, -24.95) * mm, "end": v(-41.21, -24.95) * mm});
            skLineSegment(sketch, "E37.0.8.2", {"start": v(-48.21, -24.95) * mm, "end": v(-48.21, -22.95) * mm});
            skLineSegment(sketch, "E37.0.8.3", {"start": v(-41.21, -24.95) * mm, "end": v(-41.21, -22.95) * mm});
            skLineSegment(sketch, "E37.0.9.0", {"start": v(-48.21, -18.95) * mm, "end": v(-41.21, -18.95) * mm});
            skLineSegment(sketch, "E37.0.9.1", {"start": v(-48.21, -20.95) * mm, "end": v(-41.21, -20.95) * mm});
            skLineSegment(sketch, "E37.0.9.2", {"start": v(-48.21, -20.95) * mm, "end": v(-48.21, -18.95) * mm});
            skLineSegment(sketch, "E37.0.9.3", {"start": v(-41.21, -20.95) * mm, "end": v(-41.21, -18.95) * mm});
            skLineSegment(sketch, "E37.0.10.0", {"start": v(-48.21, -14.95) * mm, "end": v(-41.21, -14.95) * mm});
            skLineSegment(sketch, "E37.0.10.1", {"start": v(-48.21, -16.95) * mm, "end": v(-41.21, -16.95) * mm});
            skLineSegment(sketch, "E37.0.10.2", {"start": v(-48.21, -16.95) * mm, "end": v(-48.21, -14.95) * mm});
            skLineSegment(sketch, "E37.0.10.3", {"start": v(-41.21, -16.95) * mm, "end": v(-41.21, -14.95) * mm});
            skLineSegment(sketch, "E37.0.11.0", {"start": v(-48.21, -10.95) * mm, "end": v(-41.21, -10.95) * mm});
            skLineSegment(sketch, "E37.0.11.1", {"start": v(-48.21, -12.95) * mm, "end": v(-41.21, -12.95) * mm});
            skLineSegment(sketch, "E37.0.11.2", {"start": v(-48.21, -12.95) * mm, "end": v(-48.21, -10.95) * mm});
            skLineSegment(sketch, "E37.0.11.3", {"start": v(-41.21, -12.95) * mm, "end": v(-41.21, -10.95) * mm});
            skLineSegment(sketch, "E37.0.12.0", {"start": v(-48.21, -6.95) * mm, "end": v(-41.21, -6.95) * mm});
            skLineSegment(sketch, "E37.0.12.1", {"start": v(-48.21, -8.95) * mm, "end": v(-41.21, -8.95) * mm});
            skLineSegment(sketch, "E37.0.12.2", {"start": v(-48.21, -8.95) * mm, "end": v(-48.21, -6.95) * mm});
            skLineSegment(sketch, "E37.0.12.3", {"start": v(-41.21, -8.95) * mm, "end": v(-41.21, -6.95) * mm});
            skLineSegment(sketch, "E37.0.13.0", {"start": v(-48.21, -2.95) * mm, "end": v(-41.21, -2.95) * mm});
            skLineSegment(sketch, "E37.0.13.1", {"start": v(-48.21, -4.95) * mm, "end": v(-41.21, -4.95) * mm});
            skLineSegment(sketch, "E37.0.13.2", {"start": v(-48.21, -4.95) * mm, "end": v(-48.21, -2.95) * mm});
            skLineSegment(sketch, "E37.0.13.3", {"start": v(-41.21, -4.95) * mm, "end": v(-41.21, -2.95) * mm});
            skLineSegment(sketch, "E37.0.14.0", {"start": v(-48.21, 1.05) * mm, "end": v(-41.21, 1.05) * mm});
            skLineSegment(sketch, "E37.0.14.1", {"start": v(-48.21, -0.95) * mm, "end": v(-41.21, -0.95) * mm});
            skLineSegment(sketch, "E37.0.14.2", {"start": v(-48.21, -0.95) * mm, "end": v(-48.21, 1.05) * mm});
            skLineSegment(sketch, "E37.0.14.3", {"start": v(-41.21, -0.95) * mm, "end": v(-41.21, 1.05) * mm});
            skLineSegment(sketch, "E37.0.15.0", {"start": v(-48.21, 5.05) * mm, "end": v(-41.21, 5.05) * mm});
            skLineSegment(sketch, "E37.0.15.1", {"start": v(-48.21, 3.05) * mm, "end": v(-41.21, 3.05) * mm});
            skLineSegment(sketch, "E37.0.15.2", {"start": v(-48.21, 3.05) * mm, "end": v(-48.21, 5.05) * mm});
            skLineSegment(sketch, "E37.0.15.3", {"start": v(-41.21, 3.05) * mm, "end": v(-41.21, 5.05) * mm});
            skLineSegment(sketch, "E37.0.16.0", {"start": v(-48.21, 9.05) * mm, "end": v(-41.21, 9.05) * mm});
            skLineSegment(sketch, "E37.0.16.1", {"start": v(-48.21, 7.05) * mm, "end": v(-41.21, 7.05) * mm});
            skLineSegment(sketch, "E37.0.16.2", {"start": v(-48.21, 7.05) * mm, "end": v(-48.21, 9.05) * mm});
            skLineSegment(sketch, "E37.0.16.3", {"start": v(-41.21, 7.05) * mm, "end": v(-41.21, 9.05) * mm});
            skLineSegment(sketch, "E37.0.17.0", {"start": v(-48.21, 13.05) * mm, "end": v(-41.21, 13.05) * mm});
            skLineSegment(sketch, "E37.0.17.1", {"start": v(-48.21, 11.05) * mm, "end": v(-41.21, 11.05) * mm});
            skLineSegment(sketch, "E37.0.17.2", {"start": v(-48.21, 11.05) * mm, "end": v(-48.21, 13.05) * mm});
            skLineSegment(sketch, "E37.0.17.3", {"start": v(-41.21, 11.05) * mm, "end": v(-41.21, 13.05) * mm});
            skLineSegment(sketch, "E37.0.18.0", {"start": v(-48.21, 17.05) * mm, "end": v(-41.21, 17.05) * mm});
            skLineSegment(sketch, "E37.0.18.1", {"start": v(-48.21, 15.05) * mm, "end": v(-41.21, 15.05) * mm});
            skLineSegment(sketch, "E37.0.18.2", {"start": v(-48.21, 15.05) * mm, "end": v(-48.21, 17.05) * mm});
            skLineSegment(sketch, "E37.0.18.3", {"start": v(-41.21, 15.05) * mm, "end": v(-41.21, 17.05) * mm});
            skLineSegment(sketch, "E37.0.19.0", {"start": v(-48.21, 21.05) * mm, "end": v(-41.21, 21.05) * mm});
            skLineSegment(sketch, "E37.0.19.1", {"start": v(-48.21, 19.05) * mm, "end": v(-41.21, 19.05) * mm});
            skLineSegment(sketch, "E37.0.19.2", {"start": v(-48.21, 19.05) * mm, "end": v(-48.21, 21.05) * mm});
            skLineSegment(sketch, "E37.0.19.3", {"start": v(-41.21, 19.05) * mm, "end": v(-41.21, 21.05) * mm});
            skLineSegment(sketch, "E37.0.20.0", {"start": v(-48.21, 25.05) * mm, "end": v(-41.21, 25.05) * mm});
            skLineSegment(sketch, "E37.0.20.1", {"start": v(-48.21, 23.05) * mm, "end": v(-41.21, 23.05) * mm});
            skLineSegment(sketch, "E37.0.20.2", {"start": v(-48.21, 23.05) * mm, "end": v(-48.21, 25.05) * mm});
            skLineSegment(sketch, "E37.0.20.3", {"start": v(-41.21, 23.05) * mm, "end": v(-41.21, 25.05) * mm});
            skLineSegment(sketch, "E37.0.21.0", {"start": v(-48.21, 29.05) * mm, "end": v(-41.21, 29.05) * mm});
            skLineSegment(sketch, "E37.0.21.1", {"start": v(-48.21, 27.05) * mm, "end": v(-41.21, 27.05) * mm});
            skLineSegment(sketch, "E37.0.21.2", {"start": v(-48.21, 27.05) * mm, "end": v(-48.21, 29.05) * mm});
            skLineSegment(sketch, "E37.0.21.3", {"start": v(-41.21, 27.05) * mm, "end": v(-41.21, 29.05) * mm});
            skLineSegment(sketch, "E37.0.22.0", {"start": v(-48.21, 33.05) * mm, "end": v(-41.21, 33.05) * mm});
            skLineSegment(sketch, "E37.0.22.1", {"start": v(-48.21, 31.05) * mm, "end": v(-41.21, 31.05) * mm});
            skLineSegment(sketch, "E37.0.22.2", {"start": v(-48.21, 31.05) * mm, "end": v(-48.21, 33.05) * mm});
            skLineSegment(sketch, "E37.0.22.3", {"start": v(-41.21, 31.05) * mm, "end": v(-41.21, 33.05) * mm});
            skLineSegment(sketch, "E37.0.23.0", {"start": v(-48.21, 37.05) * mm, "end": v(-41.21, 37.05) * mm});
            skLineSegment(sketch, "E37.0.23.1", {"start": v(-48.21, 35.05) * mm, "end": v(-41.21, 35.05) * mm});
            skLineSegment(sketch, "E37.0.23.2", {"start": v(-48.21, 35.05) * mm, "end": v(-48.21, 37.05) * mm});
            skLineSegment(sketch, "E37.0.23.3", {"start": v(-41.21, 35.05) * mm, "end": v(-41.21, 37.05) * mm});
            skLineSegment(sketch, "E37.0.24.0", {"start": v(-48.21, 41.05) * mm, "end": v(-41.21, 41.05) * mm});
            skLineSegment(sketch, "E37.0.24.1", {"start": v(-48.21, 39.05) * mm, "end": v(-41.21, 39.05) * mm});
            skLineSegment(sketch, "E37.0.24.2", {"start": v(-48.21, 39.05) * mm, "end": v(-48.21, 41.05) * mm});
            skLineSegment(sketch, "E37.0.24.3", {"start": v(-41.21, 39.05) * mm, "end": v(-41.21, 41.05) * mm});
            skLineSegment(sketch, "E37.0.25.0", {"start": v(-48.21, 45.05) * mm, "end": v(-41.21, 45.05) * mm});
            skLineSegment(sketch, "E37.0.25.1", {"start": v(-48.21, 43.05) * mm, "end": v(-41.21, 43.05) * mm});
            skLineSegment(sketch, "E37.0.25.2", {"start": v(-48.21, 43.05) * mm, "end": v(-48.21, 45.05) * mm});
            skLineSegment(sketch, "E37.0.25.3", {"start": v(-41.21, 43.05) * mm, "end": v(-41.21, 45.05) * mm});
            skLineSegment(sketch, "E37.0.26.0", {"start": v(-48.21, 49.05) * mm, "end": v(-41.21, 49.05) * mm});
            skLineSegment(sketch, "E37.0.26.1", {"start": v(-48.21, 47.05) * mm, "end": v(-41.21, 47.05) * mm});
            skLineSegment(sketch, "E37.0.26.2", {"start": v(-48.21, 47.05) * mm, "end": v(-48.21, 49.05) * mm});
            skLineSegment(sketch, "E37.0.26.3", {"start": v(-41.21, 47.05) * mm, "end": v(-41.21, 49.05) * mm});
            skLineSegment(sketch, "E37.0.27.0", {"start": v(-48.21, 53.05) * mm, "end": v(-41.21, 53.05) * mm});
            skLineSegment(sketch, "E37.0.27.1", {"start": v(-48.21, 51.05) * mm, "end": v(-41.21, 51.05) * mm});
            skLineSegment(sketch, "E37.0.27.2", {"start": v(-48.21, 51.05) * mm, "end": v(-48.21, 53.05) * mm});
            skLineSegment(sketch, "E37.0.27.3", {"start": v(-41.21, 51.05) * mm, "end": v(-41.21, 53.05) * mm});
            skLineSegment(sketch, "E37.0.28.0", {"start": v(-48.21, 57.05) * mm, "end": v(-41.21, 57.05) * mm});
            skLineSegment(sketch, "E37.0.28.1", {"start": v(-48.21, 55.05) * mm, "end": v(-41.21, 55.05) * mm});
            skLineSegment(sketch, "E37.0.28.2", {"start": v(-48.21, 55.05) * mm, "end": v(-48.21, 57.05) * mm});
            skLineSegment(sketch, "E37.0.28.3", {"start": v(-41.21, 55.05) * mm, "end": v(-41.21, 57.05) * mm});
            skLineSegment(sketch, "E37.direction1", {"start": v(-48.21, -56.95) * mm, "end": v(-40.37, -56.95) * mm, "construction": true});
            skLineSegment(sketch, "E37.direction2", {"start": v(-48.21, -56.95) * mm, "end": v(-48.21, -52.95) * mm, "construction": true});
            skLineSegment(sketch, "E38", {"start": v(0, 0) * mm, "end": v(0, 22.95) * mm, "construction": true});
            skLineSegment(sketch, "E39.MirrorCS", {"start": v(48.21, -56.95) * mm, "end": v(40.37, -56.95) * mm, "construction": true});
            skLineSegment(sketch, "E40.0.1.0", {"start": v(-40.37, -54.95) * mm, "end": v(-33.37, -54.95) * mm});
            skLineSegment(sketch, "E40.3.1.0", {"start": v(-40.37, -56.95) * mm, "end": v(-33.37, -56.95) * mm});
            skLineSegment(sketch, "E40.6.1.0", {"start": v(-40.37, -56.95) * mm, "end": v(-40.37, -54.95) * mm});
            skLineSegment(sketch, "E40.9.1.0", {"start": v(-33.37, -56.95) * mm, "end": v(-33.37, -54.95) * mm});
            skLineSegment(sketch, "E40.0.1.1", {"start": v(-40.37, -50.95) * mm, "end": v(-33.37, -50.95) * mm});
            skLineSegment(sketch, "E40.3.1.1", {"start": v(-40.37, -52.95) * mm, "end": v(-33.37, -52.95) * mm});
            skLineSegment(sketch, "E40.6.1.1", {"start": v(-40.37, -52.95) * mm, "end": v(-40.37, -50.95) * mm});
            skLineSegment(sketch, "E40.9.1.1", {"start": v(-33.37, -52.95) * mm, "end": v(-33.37, -50.95) * mm});
            skLineSegment(sketch, "E40.0.1.2", {"start": v(-40.37, -46.95) * mm, "end": v(-33.37, -46.95) * mm});
            skLineSegment(sketch, "E40.3.1.2", {"start": v(-40.37, -48.95) * mm, "end": v(-33.37, -48.95) * mm});
            skLineSegment(sketch, "E40.6.1.2", {"start": v(-40.37, -48.95) * mm, "end": v(-40.37, -46.95) * mm});
            skLineSegment(sketch, "E40.9.1.2", {"start": v(-33.37, -48.95) * mm, "end": v(-33.37, -46.95) * mm});
            skLineSegment(sketch, "E40.0.1.3", {"start": v(-40.37, -42.95) * mm, "end": v(-33.37, -42.95) * mm});
            skLineSegment(sketch, "E40.3.1.3", {"start": v(-40.37, -44.95) * mm, "end": v(-33.37, -44.95) * mm});
            skLineSegment(sketch, "E40.6.1.3", {"start": v(-40.37, -44.95) * mm, "end": v(-40.37, -42.95) * mm});
            skLineSegment(sketch, "E40.9.1.3", {"start": v(-33.37, -44.95) * mm, "end": v(-33.37, -42.95) * mm});
            skLineSegment(sketch, "E40.0.1.4", {"start": v(-40.37, -38.95) * mm, "end": v(-33.37, -38.95) * mm});
            skLineSegment(sketch, "E40.3.1.4", {"start": v(-40.37, -40.95) * mm, "end": v(-33.37, -40.95) * mm});
            skLineSegment(sketch, "E40.6.1.4", {"start": v(-40.37, -40.95) * mm, "end": v(-40.37, -38.95) * mm});
            skLineSegment(sketch, "E40.9.1.4", {"start": v(-33.37, -40.95) * mm, "end": v(-33.37, -38.95) * mm});
            skLineSegment(sketch, "E40.0.1.5", {"start": v(-40.37, -34.95) * mm, "end": v(-33.37, -34.95) * mm});
            skLineSegment(sketch, "E40.3.1.5", {"start": v(-40.37, -36.95) * mm, "end": v(-33.37, -36.95) * mm});
            skLineSegment(sketch, "E40.6.1.5", {"start": v(-40.37, -36.95) * mm, "end": v(-40.37, -34.95) * mm});
            skLineSegment(sketch, "E40.9.1.5", {"start": v(-33.37, -36.95) * mm, "end": v(-33.37, -34.95) * mm});
            skLineSegment(sketch, "E40.0.1.6", {"start": v(-40.37, -30.95) * mm, "end": v(-33.37, -30.95) * mm});
            skLineSegment(sketch, "E40.3.1.6", {"start": v(-40.37, -32.95) * mm, "end": v(-33.37, -32.95) * mm});
            skLineSegment(sketch, "E40.6.1.6", {"start": v(-40.37, -32.95) * mm, "end": v(-40.37, -30.95) * mm});
            skLineSegment(sketch, "E40.9.1.6", {"start": v(-33.37, -32.95) * mm, "end": v(-33.37, -30.95) * mm});
            skLineSegment(sketch, "E40.0.1.7", {"start": v(-40.37, -26.95) * mm, "end": v(-33.37, -26.95) * mm});
            skLineSegment(sketch, "E40.3.1.7", {"start": v(-40.37, -28.95) * mm, "end": v(-33.37, -28.95) * mm});
            skLineSegment(sketch, "E40.6.1.7", {"start": v(-40.37, -28.95) * mm, "end": v(-40.37, -26.95) * mm});
            skLineSegment(sketch, "E40.9.1.7", {"start": v(-33.37, -28.95) * mm, "end": v(-33.37, -26.95) * mm});
            skLineSegment(sketch, "E40.0.1.8", {"start": v(-40.37, -22.95) * mm, "end": v(-33.37, -22.95) * mm});
            skLineSegment(sketch, "E40.3.1.8", {"start": v(-40.37, -24.95) * mm, "end": v(-33.37, -24.95) * mm});
            skLineSegment(sketch, "E40.6.1.8", {"start": v(-40.37, -24.95) * mm, "end": v(-40.37, -22.95) * mm});
            skLineSegment(sketch, "E40.9.1.8", {"start": v(-33.37, -24.95) * mm, "end": v(-33.37, -22.95) * mm});
            skLineSegment(sketch, "E40.0.1.9", {"start": v(-40.37, -18.95) * mm, "end": v(-33.37, -18.95) * mm});
            skLineSegment(sketch, "E40.3.1.9", {"start": v(-40.37, -20.95) * mm, "end": v(-33.37, -20.95) * mm});
            skLineSegment(sketch, "E40.6.1.9", {"start": v(-40.37, -20.95) * mm, "end": v(-40.37, -18.95) * mm});
            skLineSegment(sketch, "E40.9.1.9", {"start": v(-33.37, -20.95) * mm, "end": v(-33.37, -18.95) * mm});
            skLineSegment(sketch, "E40.0.1.10", {"start": v(-40.37, -14.95) * mm, "end": v(-33.37, -14.95) * mm});
            skLineSegment(sketch, "E40.3.1.10", {"start": v(-40.37, -16.95) * mm, "end": v(-33.37, -16.95) * mm});
            skLineSegment(sketch, "E40.6.1.10", {"start": v(-40.37, -16.95) * mm, "end": v(-40.37, -14.95) * mm});
            skLineSegment(sketch, "E40.9.1.10", {"start": v(-33.37, -16.95) * mm, "end": v(-33.37, -14.95) * mm});
            skLineSegment(sketch, "E40.0.1.11", {"start": v(-40.37, -10.95) * mm, "end": v(-33.37, -10.95) * mm});
            skLineSegment(sketch, "E40.3.1.11", {"start": v(-40.37, -12.95) * mm, "end": v(-33.37, -12.95) * mm});
            skLineSegment(sketch, "E40.6.1.11", {"start": v(-40.37, -12.95) * mm, "end": v(-40.37, -10.95) * mm});
            skLineSegment(sketch, "E40.9.1.11", {"start": v(-33.37, -12.95) * mm, "end": v(-33.37, -10.95) * mm});
            skLineSegment(sketch, "E40.0.1.12", {"start": v(-40.37, -6.95) * mm, "end": v(-33.37, -6.95) * mm});
            skLineSegment(sketch, "E40.3.1.12", {"start": v(-40.37, -8.95) * mm, "end": v(-33.37, -8.95) * mm});
            skLineSegment(sketch, "E40.6.1.12", {"start": v(-40.37, -8.95) * mm, "end": v(-40.37, -6.95) * mm});
            skLineSegment(sketch, "E40.9.1.12", {"start": v(-33.37, -8.95) * mm, "end": v(-33.37, -6.95) * mm});
            skLineSegment(sketch, "E40.0.1.13", {"start": v(-40.37, -2.95) * mm, "end": v(-33.37, -2.95) * mm});
            skLineSegment(sketch, "E40.3.1.13", {"start": v(-40.37, -4.95) * mm, "end": v(-33.37, -4.95) * mm});
            skLineSegment(sketch, "E40.6.1.13", {"start": v(-40.37, -4.95) * mm, "end": v(-40.37, -2.95) * mm});
            skLineSegment(sketch, "E40.9.1.13", {"start": v(-33.37, -4.95) * mm, "end": v(-33.37, -2.95) * mm});
            skLineSegment(sketch, "E40.0.1.14", {"start": v(-40.37, 1.05) * mm, "end": v(-33.37, 1.05) * mm});
            skLineSegment(sketch, "E40.3.1.14", {"start": v(-40.37, -0.95) * mm, "end": v(-33.37, -0.95) * mm});
            skLineSegment(sketch, "E40.6.1.14", {"start": v(-40.37, -0.95) * mm, "end": v(-40.37, 1.05) * mm});
            skLineSegment(sketch, "E40.9.1.14", {"start": v(-33.37, -0.95) * mm, "end": v(-33.37, 1.05) * mm});
            skLineSegment(sketch, "E40.0.1.15", {"start": v(-40.37, 5.05) * mm, "end": v(-33.37, 5.05) * mm});
            skLineSegment(sketch, "E40.3.1.15", {"start": v(-40.37, 3.05) * mm, "end": v(-33.37, 3.05) * mm});
            skLineSegment(sketch, "E40.6.1.15", {"start": v(-40.37, 3.05) * mm, "end": v(-40.37, 5.05) * mm});
            skLineSegment(sketch, "E40.9.1.15", {"start": v(-33.37, 3.05) * mm, "end": v(-33.37, 5.05) * mm});
            skLineSegment(sketch, "E40.0.1.16", {"start": v(-40.37, 9.05) * mm, "end": v(-33.37, 9.05) * mm});
            skLineSegment(sketch, "E40.3.1.16", {"start": v(-40.37, 7.05) * mm, "end": v(-33.37, 7.05) * mm});
            skLineSegment(sketch, "E40.6.1.16", {"start": v(-40.37, 7.05) * mm, "end": v(-40.37, 9.05) * mm});
            skLineSegment(sketch, "E40.9.1.16", {"start": v(-33.37, 7.05) * mm, "end": v(-33.37, 9.05) * mm});
            skLineSegment(sketch, "E40.0.1.17", {"start": v(-40.37, 13.05) * mm, "end": v(-33.37, 13.05) * mm});
            skLineSegment(sketch, "E40.3.1.17", {"start": v(-40.37, 11.05) * mm, "end": v(-33.37, 11.05) * mm});
            skLineSegment(sketch, "E40.6.1.17", {"start": v(-40.37, 11.05) * mm, "end": v(-40.37, 13.05) * mm});
            skLineSegment(sketch, "E40.9.1.17", {"start": v(-33.37, 11.05) * mm, "end": v(-33.37, 13.05) * mm});
            skLineSegment(sketch, "E40.0.1.18", {"start": v(-40.37, 17.05) * mm, "end": v(-33.37, 17.05) * mm});
            skLineSegment(sketch, "E40.3.1.18", {"start": v(-40.37, 15.05) * mm, "end": v(-33.37, 15.05) * mm});
            skLineSegment(sketch, "E40.6.1.18", {"start": v(-40.37, 15.05) * mm, "end": v(-40.37, 17.05) * mm});
            skLineSegment(sketch, "E40.9.1.18", {"start": v(-33.37, 15.05) * mm, "end": v(-33.37, 17.05) * mm});
            skLineSegment(sketch, "E40.0.1.19", {"start": v(-40.37, 21.05) * mm, "end": v(-33.37, 21.05) * mm});
            skLineSegment(sketch, "E40.3.1.19", {"start": v(-40.37, 19.05) * mm, "end": v(-33.37, 19.05) * mm});
            skLineSegment(sketch, "E40.6.1.19", {"start": v(-40.37, 19.05) * mm, "end": v(-40.37, 21.05) * mm});
            skLineSegment(sketch, "E40.9.1.19", {"start": v(-33.37, 19.05) * mm, "end": v(-33.37, 21.05) * mm});
            skLineSegment(sketch, "E40.0.1.20", {"start": v(-40.37, 25.05) * mm, "end": v(-33.37, 25.05) * mm});
            skLineSegment(sketch, "E40.3.1.20", {"start": v(-40.37, 23.05) * mm, "end": v(-33.37, 23.05) * mm});
            skLineSegment(sketch, "E40.6.1.20", {"start": v(-40.37, 23.05) * mm, "end": v(-40.37, 25.05) * mm});
            skLineSegment(sketch, "E40.9.1.20", {"start": v(-33.37, 23.05) * mm, "end": v(-33.37, 25.05) * mm});
            skLineSegment(sketch, "E40.0.1.21", {"start": v(-40.37, 29.05) * mm, "end": v(-33.37, 29.05) * mm});
            skLineSegment(sketch, "E40.3.1.21", {"start": v(-40.37, 27.05) * mm, "end": v(-33.37, 27.05) * mm});
            skLineSegment(sketch, "E40.6.1.21", {"start": v(-40.37, 27.05) * mm, "end": v(-40.37, 29.05) * mm});
            skLineSegment(sketch, "E40.9.1.21", {"start": v(-33.37, 27.05) * mm, "end": v(-33.37, 29.05) * mm});
            skLineSegment(sketch, "E40.0.1.22", {"start": v(-40.37, 33.05) * mm, "end": v(-33.37, 33.05) * mm});
            skLineSegment(sketch, "E40.3.1.22", {"start": v(-40.37, 31.05) * mm, "end": v(-33.37, 31.05) * mm});
            skLineSegment(sketch, "E40.6.1.22", {"start": v(-40.37, 31.05) * mm, "end": v(-40.37, 33.05) * mm});
            skLineSegment(sketch, "E40.9.1.22", {"start": v(-33.37, 31.05) * mm, "end": v(-33.37, 33.05) * mm});
            skLineSegment(sketch, "E40.0.1.23", {"start": v(-40.37, 37.05) * mm, "end": v(-33.37, 37.05) * mm});
            skLineSegment(sketch, "E40.3.1.23", {"start": v(-40.37, 35.05) * mm, "end": v(-33.37, 35.05) * mm});
            skLineSegment(sketch, "E40.6.1.23", {"start": v(-40.37, 35.05) * mm, "end": v(-40.37, 37.05) * mm});
            skLineSegment(sketch, "E40.9.1.23", {"start": v(-33.37, 35.05) * mm, "end": v(-33.37, 37.05) * mm});
            skLineSegment(sketch, "E40.0.1.24", {"start": v(-40.37, 41.05) * mm, "end": v(-33.37, 41.05) * mm});
            skLineSegment(sketch, "E40.3.1.24", {"start": v(-40.37, 39.05) * mm, "end": v(-33.37, 39.05) * mm});
            skLineSegment(sketch, "E40.6.1.24", {"start": v(-40.37, 39.05) * mm, "end": v(-40.37, 41.05) * mm});
            skLineSegment(sketch, "E40.9.1.24", {"start": v(-33.37, 39.05) * mm, "end": v(-33.37, 41.05) * mm});
            skLineSegment(sketch, "E40.0.1.25", {"start": v(-40.37, 45.05) * mm, "end": v(-33.37, 45.05) * mm});
            skLineSegment(sketch, "E40.3.1.25", {"start": v(-40.37, 43.05) * mm, "end": v(-33.37, 43.05) * mm});
            skLineSegment(sketch, "E40.6.1.25", {"start": v(-40.37, 43.05) * mm, "end": v(-40.37, 45.05) * mm});
            skLineSegment(sketch, "E40.9.1.25", {"start": v(-33.37, 43.05) * mm, "end": v(-33.37, 45.05) * mm});
            skLineSegment(sketch, "E40.0.1.26", {"start": v(-40.37, 49.05) * mm, "end": v(-33.37, 49.05) * mm});
            skLineSegment(sketch, "E40.3.1.26", {"start": v(-40.37, 47.05) * mm, "end": v(-33.37, 47.05) * mm});
            skLineSegment(sketch, "E40.6.1.26", {"start": v(-40.37, 47.05) * mm, "end": v(-40.37, 49.05) * mm});
            skLineSegment(sketch, "E40.9.1.26", {"start": v(-33.37, 47.05) * mm, "end": v(-33.37, 49.05) * mm});
            skLineSegment(sketch, "E40.0.1.27", {"start": v(-40.37, 53.05) * mm, "end": v(-33.37, 53.05) * mm});
            skLineSegment(sketch, "E40.3.1.27", {"start": v(-40.37, 51.05) * mm, "end": v(-33.37, 51.05) * mm});
            skLineSegment(sketch, "E40.6.1.27", {"start": v(-40.37, 51.05) * mm, "end": v(-40.37, 53.05) * mm});
            skLineSegment(sketch, "E40.9.1.27", {"start": v(-33.37, 51.05) * mm, "end": v(-33.37, 53.05) * mm});
            skLineSegment(sketch, "E40.0.1.28", {"start": v(-40.37, 57.05) * mm, "end": v(-33.37, 57.05) * mm});
            skLineSegment(sketch, "E40.3.1.28", {"start": v(-40.37, 55.05) * mm, "end": v(-33.37, 55.05) * mm});
            skLineSegment(sketch, "E40.6.1.28", {"start": v(-40.37, 55.05) * mm, "end": v(-40.37, 57.05) * mm});
            skLineSegment(sketch, "E40.9.1.28", {"start": v(-33.37, 55.05) * mm, "end": v(-33.37, 57.05) * mm});
            skLineSegment(sketch, "E40.0.2.0", {"start": v(-32.53, -54.95) * mm, "end": v(-25.53, -54.95) * mm});
            skLineSegment(sketch, "E40.3.2.0", {"start": v(-32.53, -56.95) * mm, "end": v(-25.53, -56.95) * mm});
            skLineSegment(sketch, "E40.6.2.0", {"start": v(-32.53, -56.95) * mm, "end": v(-32.53, -54.95) * mm});
            skLineSegment(sketch, "E40.9.2.0", {"start": v(-25.53, -56.95) * mm, "end": v(-25.53, -54.95) * mm});
            skLineSegment(sketch, "E40.0.2.1", {"start": v(-32.53, -50.95) * mm, "end": v(-25.53, -50.95) * mm});
            skLineSegment(sketch, "E40.3.2.1", {"start": v(-32.53, -52.95) * mm, "end": v(-25.53, -52.95) * mm});
            skLineSegment(sketch, "E40.6.2.1", {"start": v(-32.53, -52.95) * mm, "end": v(-32.53, -50.95) * mm});
            skLineSegment(sketch, "E40.9.2.1", {"start": v(-25.53, -52.95) * mm, "end": v(-25.53, -50.95) * mm});
            skLineSegment(sketch, "E40.0.2.2", {"start": v(-32.53, -46.95) * mm, "end": v(-25.53, -46.95) * mm});
            skLineSegment(sketch, "E40.3.2.2", {"start": v(-32.53, -48.95) * mm, "end": v(-25.53, -48.95) * mm});
            skLineSegment(sketch, "E40.6.2.2", {"start": v(-32.53, -48.95) * mm, "end": v(-32.53, -46.95) * mm});
            skLineSegment(sketch, "E40.9.2.2", {"start": v(-25.53, -48.95) * mm, "end": v(-25.53, -46.95) * mm});
            skLineSegment(sketch, "E40.0.2.3", {"start": v(-32.53, -42.95) * mm, "end": v(-25.53, -42.95) * mm});
            skLineSegment(sketch, "E40.3.2.3", {"start": v(-32.53, -44.95) * mm, "end": v(-25.53, -44.95) * mm});
            skLineSegment(sketch, "E40.6.2.3", {"start": v(-32.53, -44.95) * mm, "end": v(-32.53, -42.95) * mm});
            skLineSegment(sketch, "E40.9.2.3", {"start": v(-25.53, -44.95) * mm, "end": v(-25.53, -42.95) * mm});
            skLineSegment(sketch, "E40.0.2.4", {"start": v(-32.53, -38.95) * mm, "end": v(-25.53, -38.95) * mm});
            skLineSegment(sketch, "E40.3.2.4", {"start": v(-32.53, -40.95) * mm, "end": v(-25.53, -40.95) * mm});
            skLineSegment(sketch, "E40.6.2.4", {"start": v(-32.53, -40.95) * mm, "end": v(-32.53, -38.95) * mm});
            skLineSegment(sketch, "E40.9.2.4", {"start": v(-25.53, -40.95) * mm, "end": v(-25.53, -38.95) * mm});
            skLineSegment(sketch, "E40.0.2.5", {"start": v(-32.53, -34.95) * mm, "end": v(-25.53, -34.95) * mm});
            skLineSegment(sketch, "E40.3.2.5", {"start": v(-32.53, -36.95) * mm, "end": v(-25.53, -36.95) * mm});
            skLineSegment(sketch, "E40.6.2.5", {"start": v(-32.53, -36.95) * mm, "end": v(-32.53, -34.95) * mm});
            skLineSegment(sketch, "E40.9.2.5", {"start": v(-25.53, -36.95) * mm, "end": v(-25.53, -34.95) * mm});
            skLineSegment(sketch, "E40.0.2.6", {"start": v(-32.53, -30.95) * mm, "end": v(-25.53, -30.95) * mm});
            skLineSegment(sketch, "E40.3.2.6", {"start": v(-32.53, -32.95) * mm, "end": v(-25.53, -32.95) * mm});
            skLineSegment(sketch, "E40.6.2.6", {"start": v(-32.53, -32.95) * mm, "end": v(-32.53, -30.95) * mm});
            skLineSegment(sketch, "E40.9.2.6", {"start": v(-25.53, -32.95) * mm, "end": v(-25.53, -30.95) * mm});
            skLineSegment(sketch, "E40.0.2.7", {"start": v(-32.53, -26.95) * mm, "end": v(-25.53, -26.95) * mm});
            skLineSegment(sketch, "E40.3.2.7", {"start": v(-32.53, -28.95) * mm, "end": v(-25.53, -28.95) * mm});
            skLineSegment(sketch, "E40.6.2.7", {"start": v(-32.53, -28.95) * mm, "end": v(-32.53, -26.95) * mm});
            skLineSegment(sketch, "E40.9.2.7", {"start": v(-25.53, -28.95) * mm, "end": v(-25.53, -26.95) * mm});
            skLineSegment(sketch, "E40.0.2.8", {"start": v(-32.53, -22.95) * mm, "end": v(-25.53, -22.95) * mm});
            skLineSegment(sketch, "E40.3.2.8", {"start": v(-32.53, -24.95) * mm, "end": v(-25.53, -24.95) * mm});
            skLineSegment(sketch, "E40.6.2.8", {"start": v(-32.53, -24.95) * mm, "end": v(-32.53, -22.95) * mm});
            skLineSegment(sketch, "E40.9.2.8", {"start": v(-25.53, -24.95) * mm, "end": v(-25.53, -22.95) * mm});
            skLineSegment(sketch, "E40.0.2.9", {"start": v(-32.53, -18.95) * mm, "end": v(-25.53, -18.95) * mm});
            skLineSegment(sketch, "E40.3.2.9", {"start": v(-32.53, -20.95) * mm, "end": v(-25.53, -20.95) * mm});
            skLineSegment(sketch, "E40.6.2.9", {"start": v(-32.53, -20.95) * mm, "end": v(-32.53, -18.95) * mm});
            skLineSegment(sketch, "E40.9.2.9", {"start": v(-25.53, -20.95) * mm, "end": v(-25.53, -18.95) * mm});
            skLineSegment(sketch, "E40.0.2.10", {"start": v(-32.53, -14.95) * mm, "end": v(-25.53, -14.95) * mm});
            skLineSegment(sketch, "E40.3.2.10", {"start": v(-32.53, -16.95) * mm, "end": v(-25.53, -16.95) * mm});
            skLineSegment(sketch, "E40.6.2.10", {"start": v(-32.53, -16.95) * mm, "end": v(-32.53, -14.95) * mm});
            skLineSegment(sketch, "E40.9.2.10", {"start": v(-25.53, -16.95) * mm, "end": v(-25.53, -14.95) * mm});
            skLineSegment(sketch, "E40.0.2.11", {"start": v(-32.53, -10.95) * mm, "end": v(-25.53, -10.95) * mm});
            skLineSegment(sketch, "E40.3.2.11", {"start": v(-32.53, -12.95) * mm, "end": v(-25.53, -12.95) * mm});
            skLineSegment(sketch, "E40.6.2.11", {"start": v(-32.53, -12.95) * mm, "end": v(-32.53, -10.95) * mm});
            skLineSegment(sketch, "E40.9.2.11", {"start": v(-25.53, -12.95) * mm, "end": v(-25.53, -10.95) * mm});
            skLineSegment(sketch, "E40.0.2.12", {"start": v(-32.53, -6.95) * mm, "end": v(-25.53, -6.95) * mm});
            skLineSegment(sketch, "E40.3.2.12", {"start": v(-32.53, -8.95) * mm, "end": v(-25.53, -8.95) * mm});
            skLineSegment(sketch, "E40.6.2.12", {"start": v(-32.53, -8.95) * mm, "end": v(-32.53, -6.95) * mm});
            skLineSegment(sketch, "E40.9.2.12", {"start": v(-25.53, -8.95) * mm, "end": v(-25.53, -6.95) * mm});
            skLineSegment(sketch, "E40.0.2.13", {"start": v(-32.53, -2.95) * mm, "end": v(-25.53, -2.95) * mm});
            skLineSegment(sketch, "E40.3.2.13", {"start": v(-32.53, -4.95) * mm, "end": v(-25.53, -4.95) * mm});
            skLineSegment(sketch, "E40.6.2.13", {"start": v(-32.53, -4.95) * mm, "end": v(-32.53, -2.95) * mm});
            skLineSegment(sketch, "E40.9.2.13", {"start": v(-25.53, -4.95) * mm, "end": v(-25.53, -2.95) * mm});
            skLineSegment(sketch, "E40.0.2.14", {"start": v(-32.53, 1.05) * mm, "end": v(-25.53, 1.05) * mm});
            skLineSegment(sketch, "E40.3.2.14", {"start": v(-32.53, -0.95) * mm, "end": v(-25.53, -0.95) * mm});
            skLineSegment(sketch, "E40.6.2.14", {"start": v(-32.53, -0.95) * mm, "end": v(-32.53, 1.05) * mm});
            skLineSegment(sketch, "E40.9.2.14", {"start": v(-25.53, -0.95) * mm, "end": v(-25.53, 1.05) * mm});
            skLineSegment(sketch, "E40.0.2.15", {"start": v(-32.53, 5.05) * mm, "end": v(-25.53, 5.05) * mm});
            skLineSegment(sketch, "E40.3.2.15", {"start": v(-32.53, 3.05) * mm, "end": v(-25.53, 3.05) * mm});
            skLineSegment(sketch, "E40.6.2.15", {"start": v(-32.53, 3.05) * mm, "end": v(-32.53, 5.05) * mm});
            skLineSegment(sketch, "E40.9.2.15", {"start": v(-25.53, 3.05) * mm, "end": v(-25.53, 5.05) * mm});
            skLineSegment(sketch, "E40.0.2.16", {"start": v(-32.53, 9.05) * mm, "end": v(-25.53, 9.05) * mm});
            skLineSegment(sketch, "E40.3.2.16", {"start": v(-32.53, 7.05) * mm, "end": v(-25.53, 7.05) * mm});
            skLineSegment(sketch, "E40.6.2.16", {"start": v(-32.53, 7.05) * mm, "end": v(-32.53, 9.05) * mm});
            skLineSegment(sketch, "E40.9.2.16", {"start": v(-25.53, 7.05) * mm, "end": v(-25.53, 9.05) * mm});
            skLineSegment(sketch, "E40.0.2.17", {"start": v(-32.53, 13.05) * mm, "end": v(-25.53, 13.05) * mm});
            skLineSegment(sketch, "E40.3.2.17", {"start": v(-32.53, 11.05) * mm, "end": v(-25.53, 11.05) * mm});
            skLineSegment(sketch, "E40.6.2.17", {"start": v(-32.53, 11.05) * mm, "end": v(-32.53, 13.05) * mm});
            skLineSegment(sketch, "E40.9.2.17", {"start": v(-25.53, 11.05) * mm, "end": v(-25.53, 13.05) * mm});
            skLineSegment(sketch, "E40.0.2.18", {"start": v(-32.53, 17.05) * mm, "end": v(-25.53, 17.05) * mm});
            skLineSegment(sketch, "E40.3.2.18", {"start": v(-32.53, 15.05) * mm, "end": v(-25.53, 15.05) * mm});
            skLineSegment(sketch, "E40.6.2.18", {"start": v(-32.53, 15.05) * mm, "end": v(-32.53, 17.05) * mm});
            skLineSegment(sketch, "E40.9.2.18", {"start": v(-25.53, 15.05) * mm, "end": v(-25.53, 17.05) * mm});
            skLineSegment(sketch, "E40.0.2.19", {"start": v(-32.53, 21.05) * mm, "end": v(-25.53, 21.05) * mm});
            skLineSegment(sketch, "E40.3.2.19", {"start": v(-32.53, 19.05) * mm, "end": v(-25.53, 19.05) * mm});
            skLineSegment(sketch, "E40.6.2.19", {"start": v(-32.53, 19.05) * mm, "end": v(-32.53, 21.05) * mm});
            skLineSegment(sketch, "E40.9.2.19", {"start": v(-25.53, 19.05) * mm, "end": v(-25.53, 21.05) * mm});
            skLineSegment(sketch, "E40.0.2.20", {"start": v(-32.53, 25.05) * mm, "end": v(-25.53, 25.05) * mm});
            skLineSegment(sketch, "E40.3.2.20", {"start": v(-32.53, 23.05) * mm, "end": v(-25.53, 23.05) * mm});
            skLineSegment(sketch, "E40.6.2.20", {"start": v(-32.53, 23.05) * mm, "end": v(-32.53, 25.05) * mm});
            skLineSegment(sketch, "E40.9.2.20", {"start": v(-25.53, 23.05) * mm, "end": v(-25.53, 25.05) * mm});
            skLineSegment(sketch, "E40.0.2.21", {"start": v(-32.53, 29.05) * mm, "end": v(-25.53, 29.05) * mm});
            skLineSegment(sketch, "E40.3.2.21", {"start": v(-32.53, 27.05) * mm, "end": v(-25.53, 27.05) * mm});
            skLineSegment(sketch, "E40.6.2.21", {"start": v(-32.53, 27.05) * mm, "end": v(-32.53, 29.05) * mm});
            skLineSegment(sketch, "E40.9.2.21", {"start": v(-25.53, 27.05) * mm, "end": v(-25.53, 29.05) * mm});
            skLineSegment(sketch, "E40.0.2.22", {"start": v(-32.53, 33.05) * mm, "end": v(-25.53, 33.05) * mm});
            skLineSegment(sketch, "E40.3.2.22", {"start": v(-32.53, 31.05) * mm, "end": v(-25.53, 31.05) * mm});
            skLineSegment(sketch, "E40.6.2.22", {"start": v(-32.53, 31.05) * mm, "end": v(-32.53, 33.05) * mm});
            skLineSegment(sketch, "E40.9.2.22", {"start": v(-25.53, 31.05) * mm, "end": v(-25.53, 33.05) * mm});
            skLineSegment(sketch, "E40.0.2.23", {"start": v(-32.53, 37.05) * mm, "end": v(-25.53, 37.05) * mm});
            skLineSegment(sketch, "E40.3.2.23", {"start": v(-32.53, 35.05) * mm, "end": v(-25.53, 35.05) * mm});
            skLineSegment(sketch, "E40.6.2.23", {"start": v(-32.53, 35.05) * mm, "end": v(-32.53, 37.05) * mm});
            skLineSegment(sketch, "E40.9.2.23", {"start": v(-25.53, 35.05) * mm, "end": v(-25.53, 37.05) * mm});
            skLineSegment(sketch, "E40.0.2.24", {"start": v(-32.53, 41.05) * mm, "end": v(-25.53, 41.05) * mm});
            skLineSegment(sketch, "E40.3.2.24", {"start": v(-32.53, 39.05) * mm, "end": v(-25.53, 39.05) * mm});
            skLineSegment(sketch, "E40.6.2.24", {"start": v(-32.53, 39.05) * mm, "end": v(-32.53, 41.05) * mm});
            skLineSegment(sketch, "E40.9.2.24", {"start": v(-25.53, 39.05) * mm, "end": v(-25.53, 41.05) * mm});
            skLineSegment(sketch, "E40.0.2.25", {"start": v(-32.53, 45.05) * mm, "end": v(-25.53, 45.05) * mm});
            skLineSegment(sketch, "E40.3.2.25", {"start": v(-32.53, 43.05) * mm, "end": v(-25.53, 43.05) * mm});
            skLineSegment(sketch, "E40.6.2.25", {"start": v(-32.53, 43.05) * mm, "end": v(-32.53, 45.05) * mm});
            skLineSegment(sketch, "E40.9.2.25", {"start": v(-25.53, 43.05) * mm, "end": v(-25.53, 45.05) * mm});
            skLineSegment(sketch, "E40.0.2.26", {"start": v(-32.53, 49.05) * mm, "end": v(-25.53, 49.05) * mm});
            skLineSegment(sketch, "E40.3.2.26", {"start": v(-32.53, 47.05) * mm, "end": v(-25.53, 47.05) * mm});
            skLineSegment(sketch, "E40.6.2.26", {"start": v(-32.53, 47.05) * mm, "end": v(-32.53, 49.05) * mm});
            skLineSegment(sketch, "E40.9.2.26", {"start": v(-25.53, 47.05) * mm, "end": v(-25.53, 49.05) * mm});
            skLineSegment(sketch, "E40.0.2.27", {"start": v(-32.53, 53.05) * mm, "end": v(-25.53, 53.05) * mm});
            skLineSegment(sketch, "E40.3.2.27", {"start": v(-32.53, 51.05) * mm, "end": v(-25.53, 51.05) * mm});
            skLineSegment(sketch, "E40.6.2.27", {"start": v(-32.53, 51.05) * mm, "end": v(-32.53, 53.05) * mm});
            skLineSegment(sketch, "E40.9.2.27", {"start": v(-25.53, 51.05) * mm, "end": v(-25.53, 53.05) * mm});
            skLineSegment(sketch, "E40.0.2.28", {"start": v(-32.53, 57.05) * mm, "end": v(-25.53, 57.05) * mm});
            skLineSegment(sketch, "E40.3.2.28", {"start": v(-32.53, 55.05) * mm, "end": v(-25.53, 55.05) * mm});
            skLineSegment(sketch, "E40.6.2.28", {"start": v(-32.53, 55.05) * mm, "end": v(-32.53, 57.05) * mm});
            skLineSegment(sketch, "E40.9.2.28", {"start": v(-25.53, 55.05) * mm, "end": v(-25.53, 57.05) * mm});
            skLineSegment(sketch, "E41.MirrorCS", {"start": v(48.21, -56.95) * mm, "end": v(48.21, -54.95) * mm});
            skLineSegment(sketch, "E42.MirrorCS", {"start": v(41.21, -56.95) * mm, "end": v(41.21, -54.95) * mm});
            skLineSegment(sketch, "E43.MirrorCS", {"start": v(40.37, -56.95) * mm, "end": v(40.37, -54.95) * mm});
            skLineSegment(sketch, "E44.MirrorCS", {"start": v(48.21, -56.95) * mm, "end": v(48.21, -52.95) * mm, "construction": true});
            skLineSegment(sketch, "E45.MirrorCS", {"start": v(33.37, 35.05) * mm, "end": v(33.37, 37.05) * mm});
            skLineSegment(sketch, "E46.MirrorCS", {"start": v(40.37, 7.05) * mm, "end": v(40.37, 9.05) * mm});
            skLineSegment(sketch, "E47.MirrorCS", {"start": v(25.53, -28.95) * mm, "end": v(25.53, -26.95) * mm});
            skLineSegment(sketch, "E48.MirrorCS", {"start": v(41.21, -16.95) * mm, "end": v(41.21, -14.95) * mm});
            skLineSegment(sketch, "E49.MirrorCS", {"start": v(25.53, -16.95) * mm, "end": v(25.53, -14.95) * mm});
            skLineSegment(sketch, "E50.MirrorCS", {"start": v(32.53, 19.05) * mm, "end": v(32.53, 21.05) * mm});
            skLineSegment(sketch, "E51.MirrorCS", {"start": v(32.53, -44.95) * mm, "end": v(32.53, -42.95) * mm});
            skLineSegment(sketch, "E52.MirrorCS", {"start": v(41.21, -8.95) * mm, "end": v(41.21, -6.95) * mm});
            skLineSegment(sketch, "E53.MirrorCS", {"start": v(25.53, -32.95) * mm, "end": v(25.53, -30.95) * mm});
            skLineSegment(sketch, "E54.MirrorCS", {"start": v(41.21, 35.05) * mm, "end": v(41.21, 37.05) * mm});
            skLineSegment(sketch, "E55.MirrorCS", {"start": v(40.37, -4.95) * mm, "end": v(40.37, -2.95) * mm});
            skLineSegment(sketch, "E56.MirrorCS", {"start": v(32.53, 23.05) * mm, "end": v(32.53, 25.05) * mm});
            skLineSegment(sketch, "E57.MirrorCS", {"start": v(32.53, 15.05) * mm, "end": v(32.53, 17.05) * mm});
            skLineSegment(sketch, "E58.MirrorCS", {"start": v(48.21, 3.05) * mm, "end": v(48.21, 5.05) * mm});
            skLineSegment(sketch, "E59.MirrorCS", {"start": v(40.37, -32.95) * mm, "end": v(40.37, -30.95) * mm});
            skLineSegment(sketch, "E60.MirrorCS", {"start": v(41.21, -12.95) * mm, "end": v(41.21, -10.95) * mm});
            skLineSegment(sketch, "E61.MirrorCS", {"start": v(33.37, -32.95) * mm, "end": v(33.37, -30.95) * mm});
            skLineSegment(sketch, "E62.MirrorCS", {"start": v(41.21, 55.05) * mm, "end": v(41.21, 57.05) * mm});
            skLineSegment(sketch, "E63.MirrorCS", {"start": v(40.37, -8.95) * mm, "end": v(40.37, -6.95) * mm});
            skLineSegment(sketch, "E64.MirrorCS", {"start": v(48.21, 19.05) * mm, "end": v(48.21, 21.05) * mm});
            skLineSegment(sketch, "E65.MirrorCS", {"start": v(41.21, 51.05) * mm, "end": v(41.21, 53.05) * mm});
            skLineSegment(sketch, "E66.MirrorCS", {"start": v(48.21, 35.05) * mm, "end": v(48.21, 37.05) * mm});
            skLineSegment(sketch, "E67.MirrorCS", {"start": v(32.53, -40.95) * mm, "end": v(32.53, -38.95) * mm});
            skLineSegment(sketch, "E68.MirrorCS", {"start": v(25.53, 23.05) * mm, "end": v(25.53, 25.05) * mm});
            skLineSegment(sketch, "E69.MirrorCS", {"start": v(48.21, 31.05) * mm, "end": v(48.21, 33.05) * mm});
            skLineSegment(sketch, "E70.MirrorCS", {"start": v(48.21, -4.95) * mm, "end": v(48.21, -2.95) * mm});
            skLineSegment(sketch, "E71.MirrorCS", {"start": v(25.53, -8.95) * mm, "end": v(25.53, -6.95) * mm});
            skLineSegment(sketch, "E72.MirrorCS", {"start": v(32.53, 51.05) * mm, "end": v(32.53, 53.05) * mm});
            skLineSegment(sketch, "E73.MirrorCS", {"start": v(32.53, -8.95) * mm, "end": v(32.53, -6.95) * mm});
            skLineSegment(sketch, "E74.MirrorCS", {"start": v(32.53, 47.05) * mm, "end": v(32.53, 49.05) * mm});
            skLineSegment(sketch, "E75.MirrorCS", {"start": v(33.37, -8.95) * mm, "end": v(33.37, -6.95) * mm});
            skLineSegment(sketch, "E76.MirrorCS", {"start": v(48.21, -48.95) * mm, "end": v(48.21, -46.95) * mm});
            skLineSegment(sketch, "E77.MirrorCS", {"start": v(41.21, 43.05) * mm, "end": v(41.21, 45.05) * mm});
            skLineSegment(sketch, "E78.MirrorCS", {"start": v(32.53, 3.05) * mm, "end": v(32.53, 5.05) * mm});
            skLineSegment(sketch, "E79.MirrorCS", {"start": v(25.53, 43.05) * mm, "end": v(25.53, 45.05) * mm});
            skLineSegment(sketch, "E80.MirrorCS", {"start": v(32.53, 39.05) * mm, "end": v(32.53, 41.05) * mm});
            skLineSegment(sketch, "E81.MirrorCS", {"start": v(25.53, -48.95) * mm, "end": v(25.53, -46.95) * mm});
            skLineSegment(sketch, "E82.MirrorCS", {"start": v(33.37, 11.05) * mm, "end": v(33.37, 13.05) * mm});
            skLineSegment(sketch, "E83.MirrorCS", {"start": v(25.53, -36.95) * mm, "end": v(25.53, -34.95) * mm});
            skLineSegment(sketch, "E84.MirrorCS", {"start": v(48.21, -0.95) * mm, "end": v(48.21, 1.05) * mm});
            skLineSegment(sketch, "E85.MirrorCS", {"start": v(48.21, 51.05) * mm, "end": v(48.21, 53.05) * mm});
            skLineSegment(sketch, "E86.MirrorCS", {"start": v(40.37, 55.05) * mm, "end": v(40.37, 57.05) * mm});
            skLineSegment(sketch, "E87.MirrorCS", {"start": v(41.21, -32.95) * mm, "end": v(41.21, -30.95) * mm});
            skLineSegment(sketch, "E88.MirrorCS", {"start": v(25.53, 31.05) * mm, "end": v(25.53, 33.05) * mm});
            skLineSegment(sketch, "E89.MirrorCS", {"start": v(33.37, 47.05) * mm, "end": v(33.37, 49.05) * mm});
            skLineSegment(sketch, "E90.MirrorCS", {"start": v(33.37, -20.95) * mm, "end": v(33.37, -18.95) * mm});
            skLineSegment(sketch, "E91.MirrorCS", {"start": v(32.53, -52.95) * mm, "end": v(32.53, -50.95) * mm});
            skLineSegment(sketch, "E92.MirrorCS", {"start": v(33.37, -24.95) * mm, "end": v(33.37, -22.95) * mm});
            skLineSegment(sketch, "E93.MirrorCS", {"start": v(32.53, -32.95) * mm, "end": v(32.53, -30.95) * mm});
            skLineSegment(sketch, "E94.MirrorCS", {"start": v(40.37, -28.95) * mm, "end": v(40.37, -26.95) * mm});
            skLineSegment(sketch, "E95.MirrorCS", {"start": v(33.37, 55.05) * mm, "end": v(33.37, 57.05) * mm});
            skLineSegment(sketch, "E96.MirrorCS", {"start": v(48.21, -28.95) * mm, "end": v(48.21, -26.95) * mm});
            skLineSegment(sketch, "E97.MirrorCS", {"start": v(40.37, -24.95) * mm, "end": v(40.37, -22.95) * mm});
            skLineSegment(sketch, "E98.MirrorCS", {"start": v(41.21, 19.05) * mm, "end": v(41.21, 21.05) * mm});
            skLineSegment(sketch, "E99.MirrorCS", {"start": v(25.53, -56.95) * mm, "end": v(25.53, -54.95) * mm});
            skLineSegment(sketch, "E100.MirrorCS", {"start": v(25.53, 11.05) * mm, "end": v(25.53, 13.05) * mm});
            skLineSegment(sketch, "E101.MirrorCS", {"start": v(48.21, -12.95) * mm, "end": v(48.21, -10.95) * mm});
            skLineSegment(sketch, "E102.MirrorCS", {"start": v(25.53, -24.95) * mm, "end": v(25.53, -22.95) * mm});
            skLineSegment(sketch, "E103.MirrorCS", {"start": v(32.53, 43.05) * mm, "end": v(32.53, 45.05) * mm});
            skLineSegment(sketch, "E104.MirrorCS", {"start": v(40.37, -36.95) * mm, "end": v(40.37, -34.95) * mm});
            skLineSegment(sketch, "E105.MirrorCS", {"start": v(41.21, -0.95) * mm, "end": v(41.21, 1.05) * mm});
            skLineSegment(sketch, "E106.MirrorCS", {"start": v(25.53, 7.05) * mm, "end": v(25.53, 9.05) * mm});
            skLineSegment(sketch, "E107.MirrorCS", {"start": v(48.21, 47.05) * mm, "end": v(48.21, 49.05) * mm});
            skLineSegment(sketch, "E108.MirrorCS", {"start": v(32.53, -36.95) * mm, "end": v(32.53, -34.95) * mm});
            skLineSegment(sketch, "E109.MirrorCS", {"start": v(25.53, 39.05) * mm, "end": v(25.53, 41.05) * mm});
            skLineSegment(sketch, "E110.MirrorCS", {"start": v(41.21, 3.05) * mm, "end": v(41.21, 5.05) * mm});
            skLineSegment(sketch, "E111.MirrorCS", {"start": v(41.21, -20.95) * mm, "end": v(41.21, -18.95) * mm});
            skLineSegment(sketch, "E112.MirrorCS", {"start": v(33.37, 15.05) * mm, "end": v(33.37, 17.05) * mm});
            skLineSegment(sketch, "E113.MirrorCS", {"start": v(41.21, 39.05) * mm, "end": v(41.21, 41.05) * mm});
            skLineSegment(sketch, "E114.MirrorCS", {"start": v(40.37, -12.95) * mm, "end": v(40.37, -10.95) * mm});
            skLineSegment(sketch, "E115.MirrorCS", {"start": v(40.37, -16.95) * mm, "end": v(40.37, -14.95) * mm});
            skLineSegment(sketch, "E116.MirrorCS", {"start": v(48.21, -16.95) * mm, "end": v(48.21, -14.95) * mm});
            skLineSegment(sketch, "E117.MirrorCS", {"start": v(41.21, -40.95) * mm, "end": v(41.21, -38.95) * mm});
            skLineSegment(sketch, "E118.MirrorCS", {"start": v(48.21, 7.05) * mm, "end": v(48.21, 9.05) * mm});
            skLineSegment(sketch, "E119.MirrorCS", {"start": v(41.21, -24.95) * mm, "end": v(41.21, -22.95) * mm});
            skLineSegment(sketch, "E120.MirrorCS", {"start": v(32.53, -20.95) * mm, "end": v(32.53, -18.95) * mm});
            skLineSegment(sketch, "E121.MirrorCS", {"start": v(40.37, 11.05) * mm, "end": v(40.37, 13.05) * mm});
            skLineSegment(sketch, "E122.MirrorCS", {"start": v(48.21, -44.95) * mm, "end": v(48.21, -42.95) * mm});
            skLineSegment(sketch, "E123.MirrorCS", {"start": v(41.21, -28.95) * mm, "end": v(41.21, -26.95) * mm});
            skLineSegment(sketch, "E124.MirrorCS", {"start": v(32.53, 31.05) * mm, "end": v(32.53, 33.05) * mm});
            skLineSegment(sketch, "E125.MirrorCS", {"start": v(32.53, -48.95) * mm, "end": v(32.53, -46.95) * mm});
            skLineSegment(sketch, "E126.MirrorCS", {"start": v(41.21, 15.05) * mm, "end": v(41.21, 17.05) * mm});
            skLineSegment(sketch, "E127.MirrorCS", {"start": v(33.37, 27.05) * mm, "end": v(33.37, 29.05) * mm});
            skLineSegment(sketch, "E128.MirrorCS", {"start": v(40.37, 35.05) * mm, "end": v(40.37, 37.05) * mm});
            skLineSegment(sketch, "E129.MirrorCS", {"start": v(48.21, 27.05) * mm, "end": v(48.21, 29.05) * mm});
            skLineSegment(sketch, "E130.MirrorCS", {"start": v(40.37, 27.05) * mm, "end": v(40.37, 29.05) * mm});
            skLineSegment(sketch, "E131.MirrorCS", {"start": v(32.53, -4.95) * mm, "end": v(32.53, -2.95) * mm});
            skLineSegment(sketch, "E132.MirrorCS", {"start": v(40.37, 15.05) * mm, "end": v(40.37, 17.05) * mm});
            skLineSegment(sketch, "E133.MirrorCS", {"start": v(48.21, -24.95) * mm, "end": v(48.21, -22.95) * mm});
            skLineSegment(sketch, "E134.MirrorCS", {"start": v(48.21, 43.05) * mm, "end": v(48.21, 45.05) * mm});
            skLineSegment(sketch, "E135.MirrorCS", {"start": v(40.37, 3.05) * mm, "end": v(40.37, 5.05) * mm});
            skLineSegment(sketch, "E136.MirrorCS", {"start": v(32.53, -24.95) * mm, "end": v(32.53, -22.95) * mm});
            skLineSegment(sketch, "E137.MirrorCS", {"start": v(40.37, -20.95) * mm, "end": v(40.37, -18.95) * mm});
            skLineSegment(sketch, "E138.MirrorCS", {"start": v(48.21, 55.05) * mm, "end": v(48.21, 57.05) * mm});
            skLineSegment(sketch, "E139.MirrorCS", {"start": v(33.37, -4.95) * mm, "end": v(33.37, -2.95) * mm});
            skLineSegment(sketch, "E140.MirrorCS", {"start": v(25.53, -20.95) * mm, "end": v(25.53, -18.95) * mm});
            skLineSegment(sketch, "E141.MirrorCS", {"start": v(25.53, 55.05) * mm, "end": v(25.53, 57.05) * mm});
            skLineSegment(sketch, "E142.MirrorCS", {"start": v(25.53, 35.05) * mm, "end": v(25.53, 37.05) * mm});
            skLineSegment(sketch, "E143.MirrorCS", {"start": v(33.37, -12.95) * mm, "end": v(33.37, -10.95) * mm});
            skLineSegment(sketch, "E144.MirrorCS", {"start": v(33.37, -40.95) * mm, "end": v(33.37, -38.95) * mm});
            skLineSegment(sketch, "E145.MirrorCS", {"start": v(41.21, 31.05) * mm, "end": v(41.21, 33.05) * mm});
            skLineSegment(sketch, "E146.MirrorCS", {"start": v(48.21, 23.05) * mm, "end": v(48.21, 25.05) * mm});
            skLineSegment(sketch, "E147.MirrorCS", {"start": v(33.37, -36.95) * mm, "end": v(33.37, -34.95) * mm});
            skLineSegment(sketch, "E148.MirrorCS", {"start": v(33.37, 3.05) * mm, "end": v(33.37, 5.05) * mm});
            skLineSegment(sketch, "E149.MirrorCS", {"start": v(40.37, 43.05) * mm, "end": v(40.37, 45.05) * mm});
            skLineSegment(sketch, "E150.MirrorCS", {"start": v(32.53, -0.95) * mm, "end": v(32.53, 1.05) * mm});
            skLineSegment(sketch, "E151.MirrorCS", {"start": v(25.53, 19.05) * mm, "end": v(25.53, 21.05) * mm});
            skLineSegment(sketch, "E152.MirrorCS", {"start": v(25.53, 3.05) * mm, "end": v(25.53, 5.05) * mm});
            skLineSegment(sketch, "E153.MirrorCS", {"start": v(33.37, 7.05) * mm, "end": v(33.37, 9.05) * mm});
            skLineSegment(sketch, "E154.MirrorCS", {"start": v(41.21, -52.95) * mm, "end": v(41.21, -50.95) * mm});
            skLineSegment(sketch, "E155.MirrorCS", {"start": v(41.21, 11.05) * mm, "end": v(41.21, 13.05) * mm});
            skLineSegment(sketch, "E156.MirrorCS", {"start": v(41.21, 47.05) * mm, "end": v(41.21, 49.05) * mm});
            skLineSegment(sketch, "E157.MirrorCS", {"start": v(25.53, -40.95) * mm, "end": v(25.53, -38.95) * mm});
            skLineSegment(sketch, "E158.MirrorCS", {"start": v(41.21, 23.05) * mm, "end": v(41.21, 25.05) * mm});
            skLineSegment(sketch, "E159.MirrorCS", {"start": v(48.21, 39.05) * mm, "end": v(48.21, 41.05) * mm});
            skLineSegment(sketch, "E160.MirrorCS", {"start": v(40.37, 39.05) * mm, "end": v(40.37, 41.05) * mm});
            skLineSegment(sketch, "E161.MirrorCS", {"start": v(40.37, -48.95) * mm, "end": v(40.37, -46.95) * mm});
            skLineSegment(sketch, "E162.MirrorCS", {"start": v(25.53, 47.05) * mm, "end": v(25.53, 49.05) * mm});
            skLineSegment(sketch, "E163.MirrorCS", {"start": v(25.53, -4.95) * mm, "end": v(25.53, -2.95) * mm});
            skLineSegment(sketch, "E164.MirrorCS", {"start": v(33.37, 31.05) * mm, "end": v(33.37, 33.05) * mm});
            skLineSegment(sketch, "E165.MirrorCS", {"start": v(32.53, 55.05) * mm, "end": v(32.53, 57.05) * mm});
            skLineSegment(sketch, "E166.MirrorCS", {"start": v(33.37, -16.95) * mm, "end": v(33.37, -14.95) * mm});
            skLineSegment(sketch, "E167.MirrorCS", {"start": v(41.21, -44.95) * mm, "end": v(41.21, -42.95) * mm});
            skLineSegment(sketch, "E168.MirrorCS", {"start": v(33.37, 23.05) * mm, "end": v(33.37, 25.05) * mm});
            skLineSegment(sketch, "E169.MirrorCS", {"start": v(48.21, 15.05) * mm, "end": v(48.21, 17.05) * mm});
            skLineSegment(sketch, "E170.MirrorCS", {"start": v(33.37, 39.05) * mm, "end": v(33.37, 41.05) * mm});
            skLineSegment(sketch, "E171.MirrorCS", {"start": v(41.21, -4.95) * mm, "end": v(41.21, -2.95) * mm});
            skLineSegment(sketch, "E172.MirrorCS", {"start": v(40.37, 47.05) * mm, "end": v(40.37, 49.05) * mm});
            skLineSegment(sketch, "E173.MirrorCS", {"start": v(48.21, -40.95) * mm, "end": v(48.21, -38.95) * mm});
            skLineSegment(sketch, "E174.MirrorCS", {"start": v(48.21, -8.95) * mm, "end": v(48.21, -6.95) * mm});
            skLineSegment(sketch, "E175.MirrorCS", {"start": v(25.53, -52.95) * mm, "end": v(25.53, -50.95) * mm});
            skLineSegment(sketch, "E176.MirrorCS", {"start": v(41.21, 7.05) * mm, "end": v(41.21, 9.05) * mm});
            skLineSegment(sketch, "E177.MirrorCS", {"start": v(32.53, -56.95) * mm, "end": v(32.53, -54.95) * mm});
            skLineSegment(sketch, "E178.MirrorCS", {"start": v(33.37, -52.95) * mm, "end": v(33.37, -50.95) * mm});
            skLineSegment(sketch, "E179.MirrorCS", {"start": v(48.21, -32.95) * mm, "end": v(48.21, -30.95) * mm});
            skLineSegment(sketch, "E180.MirrorCS", {"start": v(25.53, -0.95) * mm, "end": v(25.53, 1.05) * mm});
            skLineSegment(sketch, "E181.MirrorCS", {"start": v(33.37, -56.95) * mm, "end": v(33.37, -54.95) * mm});
            skLineSegment(sketch, "E182.MirrorCS", {"start": v(32.53, 7.05) * mm, "end": v(32.53, 9.05) * mm});
            skLineSegment(sketch, "E183.MirrorCS", {"start": v(32.53, -16.95) * mm, "end": v(32.53, -14.95) * mm});
            skLineSegment(sketch, "E184.MirrorCS", {"start": v(32.53, 11.05) * mm, "end": v(32.53, 13.05) * mm});
            skLineSegment(sketch, "E185.MirrorCS", {"start": v(25.53, 15.05) * mm, "end": v(25.53, 17.05) * mm});
            skLineSegment(sketch, "E186.MirrorCS", {"start": v(40.37, 51.05) * mm, "end": v(40.37, 53.05) * mm});
            skLineSegment(sketch, "E187.MirrorCS", {"start": v(40.37, -40.95) * mm, "end": v(40.37, -38.95) * mm});
            skLineSegment(sketch, "E188.MirrorCS", {"start": v(41.21, 27.05) * mm, "end": v(41.21, 29.05) * mm});
            skLineSegment(sketch, "E189.MirrorCS", {"start": v(40.37, -0.95) * mm, "end": v(40.37, 1.05) * mm});
            skLineSegment(sketch, "E190.MirrorCS", {"start": v(48.21, -52.95) * mm, "end": v(48.21, -50.95) * mm});
            skLineSegment(sketch, "E191.MirrorCS", {"start": v(33.37, -28.95) * mm, "end": v(33.37, -26.95) * mm});
            skLineSegment(sketch, "E192.MirrorCS", {"start": v(33.37, -48.95) * mm, "end": v(33.37, -46.95) * mm});
            skLineSegment(sketch, "E193.MirrorCS", {"start": v(40.37, 31.05) * mm, "end": v(40.37, 33.05) * mm});
            skLineSegment(sketch, "E194.MirrorCS", {"start": v(48.21, 11.05) * mm, "end": v(48.21, 13.05) * mm});
            skLineSegment(sketch, "E195.MirrorCS", {"start": v(33.37, 43.05) * mm, "end": v(33.37, 45.05) * mm});
            skLineSegment(sketch, "E196.MirrorCS", {"start": v(25.53, 51.05) * mm, "end": v(25.53, 53.05) * mm});
            skLineSegment(sketch, "E197.MirrorCS", {"start": v(48.21, -20.95) * mm, "end": v(48.21, -18.95) * mm});
            skLineSegment(sketch, "E198.MirrorCS", {"start": v(48.21, -36.95) * mm, "end": v(48.21, -34.95) * mm});
            skLineSegment(sketch, "E199.MirrorCS", {"start": v(32.53, 35.05) * mm, "end": v(32.53, 37.05) * mm});
            skLineSegment(sketch, "E200.MirrorCS", {"start": v(32.53, 27.05) * mm, "end": v(32.53, 29.05) * mm});
            skLineSegment(sketch, "E201.MirrorCS", {"start": v(25.53, -12.95) * mm, "end": v(25.53, -10.95) * mm});
            skLineSegment(sketch, "E202.MirrorCS", {"start": v(32.53, -28.95) * mm, "end": v(32.53, -26.95) * mm});
            skLineSegment(sketch, "E203.MirrorCS", {"start": v(40.37, -52.95) * mm, "end": v(40.37, -50.95) * mm});
            skLineSegment(sketch, "E204.MirrorCS", {"start": v(33.37, -0.95) * mm, "end": v(33.37, 1.05) * mm});
            skLineSegment(sketch, "E205.MirrorCS", {"start": v(25.53, -44.95) * mm, "end": v(25.53, -42.95) * mm});
            skLineSegment(sketch, "E206.MirrorCS", {"start": v(40.37, -44.95) * mm, "end": v(40.37, -42.95) * mm});
            skLineSegment(sketch, "E207.MirrorCS", {"start": v(41.21, -36.95) * mm, "end": v(41.21, -34.95) * mm});
            skLineSegment(sketch, "E208.MirrorCS", {"start": v(40.37, 19.05) * mm, "end": v(40.37, 21.05) * mm});
            skLineSegment(sketch, "E209.MirrorCS", {"start": v(40.37, 23.05) * mm, "end": v(40.37, 25.05) * mm});
            skLineSegment(sketch, "E210.MirrorCS", {"start": v(33.37, 51.05) * mm, "end": v(33.37, 53.05) * mm});
            skLineSegment(sketch, "E211.MirrorCS", {"start": v(33.37, -44.95) * mm, "end": v(33.37, -42.95) * mm});
            skLineSegment(sketch, "E212.MirrorCS", {"start": v(25.53, 27.05) * mm, "end": v(25.53, 29.05) * mm});
            skLineSegment(sketch, "E213.MirrorCS", {"start": v(32.53, -12.95) * mm, "end": v(32.53, -10.95) * mm});
            skLineSegment(sketch, "E214.MirrorCS", {"start": v(41.21, -48.95) * mm, "end": v(41.21, -46.95) * mm});
            skLineSegment(sketch, "E215.MirrorCS", {"start": v(33.37, 19.05) * mm, "end": v(33.37, 21.05) * mm});
            skLineSegment(sketch, "E216.MirrorCS", {"start": v(32.53, -16.95) * mm, "end": v(25.53, -16.95) * mm});
            skLineSegment(sketch, "E217.MirrorCS", {"start": v(32.53, 25.05) * mm, "end": v(25.53, 25.05) * mm});
            skLineSegment(sketch, "E218.MirrorCS", {"start": v(32.53, -14.95) * mm, "end": v(25.53, -14.95) * mm});
            skLineSegment(sketch, "E219.MirrorCS", {"start": v(48.21, 45.05) * mm, "end": v(41.21, 45.05) * mm});
            skLineSegment(sketch, "E220.MirrorCS", {"start": v(40.37, 19.05) * mm, "end": v(33.37, 19.05) * mm});
            skLineSegment(sketch, "E221.MirrorCS", {"start": v(32.53, -34.95) * mm, "end": v(25.53, -34.95) * mm});
            skLineSegment(sketch, "E222.MirrorCS", {"start": v(40.37, 49.05) * mm, "end": v(33.37, 49.05) * mm});
            skLineSegment(sketch, "E223.MirrorCS", {"start": v(32.53, -32.95) * mm, "end": v(25.53, -32.95) * mm});
            skLineSegment(sketch, "E224.MirrorCS", {"start": v(40.37, -10.95) * mm, "end": v(33.37, -10.95) * mm});
            skLineSegment(sketch, "E225.MirrorCS", {"start": v(40.37, -22.95) * mm, "end": v(33.37, -22.95) * mm});
            skLineSegment(sketch, "E226.MirrorCS", {"start": v(40.37, 55.05) * mm, "end": v(33.37, 55.05) * mm});
            skLineSegment(sketch, "E227.MirrorCS", {"start": v(40.37, 23.05) * mm, "end": v(33.37, 23.05) * mm});
            skLineSegment(sketch, "E228.MirrorCS", {"start": v(32.53, -44.95) * mm, "end": v(25.53, -44.95) * mm});
            skLineSegment(sketch, "E229.MirrorCS", {"start": v(48.21, 29.05) * mm, "end": v(41.21, 29.05) * mm});
            skLineSegment(sketch, "E230.MirrorCS", {"start": v(48.21, -24.95) * mm, "end": v(41.21, -24.95) * mm});
            skLineSegment(sketch, "E231.MirrorCS", {"start": v(32.53, 33.05) * mm, "end": v(25.53, 33.05) * mm});
            skLineSegment(sketch, "E232.MirrorCS", {"start": v(40.37, -4.95) * mm, "end": v(33.37, -4.95) * mm});
            skLineSegment(sketch, "E233.MirrorCS", {"start": v(48.21, 47.05) * mm, "end": v(41.21, 47.05) * mm});
            skLineSegment(sketch, "E234.MirrorCS", {"start": v(48.21, 53.05) * mm, "end": v(41.21, 53.05) * mm});
            skLineSegment(sketch, "E235.MirrorCS", {"start": v(32.53, 17.05) * mm, "end": v(25.53, 17.05) * mm});
            skLineSegment(sketch, "E236.MirrorCS", {"start": v(40.37, -30.95) * mm, "end": v(33.37, -30.95) * mm});
            skLineSegment(sketch, "E237.MirrorCS", {"start": v(48.21, -28.95) * mm, "end": v(41.21, -28.95) * mm});
            skLineSegment(sketch, "E238.MirrorCS", {"start": v(40.37, -54.95) * mm, "end": v(33.37, -54.95) * mm});
            skLineSegment(sketch, "E239.MirrorCS", {"start": v(32.53, 55.05) * mm, "end": v(25.53, 55.05) * mm});
            skLineSegment(sketch, "E240.MirrorCS", {"start": v(32.53, 31.05) * mm, "end": v(25.53, 31.05) * mm});
            skLineSegment(sketch, "E241.MirrorCS", {"start": v(48.21, 39.05) * mm, "end": v(41.21, 39.05) * mm});
            skLineSegment(sketch, "E242.MirrorCS", {"start": v(48.21, -46.95) * mm, "end": v(41.21, -46.95) * mm});
            skLineSegment(sketch, "E243.MirrorCS", {"start": v(40.37, -0.95) * mm, "end": v(33.37, -0.95) * mm});
            skLineSegment(sketch, "E244.MirrorCS", {"start": v(48.21, -54.95) * mm, "end": v(41.21, -54.95) * mm});
            skLineSegment(sketch, "E245.MirrorCS", {"start": v(48.21, -50.95) * mm, "end": v(41.21, -50.95) * mm});
            skLineSegment(sketch, "E246.MirrorCS", {"start": v(48.21, 51.05) * mm, "end": v(41.21, 51.05) * mm});
            skLineSegment(sketch, "E247.MirrorCS", {"start": v(32.53, -22.95) * mm, "end": v(25.53, -22.95) * mm});
            skLineSegment(sketch, "E248.MirrorCS", {"start": v(48.21, -42.95) * mm, "end": v(41.21, -42.95) * mm});
            skLineSegment(sketch, "E249.MirrorCS", {"start": v(40.37, 33.05) * mm, "end": v(33.37, 33.05) * mm});
            skLineSegment(sketch, "E250.MirrorCS", {"start": v(48.21, -20.95) * mm, "end": v(41.21, -20.95) * mm});
            skLineSegment(sketch, "E251.MirrorCS", {"start": v(40.37, -12.95) * mm, "end": v(33.37, -12.95) * mm});
            skLineSegment(sketch, "E252.MirrorCS", {"start": v(48.21, 7.05) * mm, "end": v(41.21, 7.05) * mm});
            skLineSegment(sketch, "E253.MirrorCS", {"start": v(48.21, -18.95) * mm, "end": v(41.21, -18.95) * mm});
            skLineSegment(sketch, "E254.MirrorCS", {"start": v(48.21, -40.95) * mm, "end": v(41.21, -40.95) * mm});
            skLineSegment(sketch, "E255.MirrorCS", {"start": v(32.53, -40.95) * mm, "end": v(25.53, -40.95) * mm});
            skLineSegment(sketch, "E256.MirrorCS", {"start": v(40.37, 15.05) * mm, "end": v(33.37, 15.05) * mm});
            skLineSegment(sketch, "E257.MirrorCS", {"start": v(48.21, -22.95) * mm, "end": v(41.21, -22.95) * mm});
            skLineSegment(sketch, "E258.MirrorCS", {"start": v(32.53, 3.05) * mm, "end": v(25.53, 3.05) * mm});
            skLineSegment(sketch, "E259.MirrorCS", {"start": v(48.21, -6.95) * mm, "end": v(41.21, -6.95) * mm});
            skLineSegment(sketch, "E260.MirrorCS", {"start": v(40.37, -6.95) * mm, "end": v(33.37, -6.95) * mm});
            skLineSegment(sketch, "E261.MirrorCS", {"start": v(48.21, 23.05) * mm, "end": v(41.21, 23.05) * mm});
            skLineSegment(sketch, "E262.MirrorCS", {"start": v(40.37, 45.05) * mm, "end": v(33.37, 45.05) * mm});
            skLineSegment(sketch, "E263.MirrorCS", {"start": v(48.21, -2.95) * mm, "end": v(41.21, -2.95) * mm});
            skLineSegment(sketch, "E264.MirrorCS", {"start": v(32.53, 45.05) * mm, "end": v(25.53, 45.05) * mm});
            skLineSegment(sketch, "E265.MirrorCS", {"start": v(32.53, -18.95) * mm, "end": v(25.53, -18.95) * mm});
            skLineSegment(sketch, "E266.MirrorCS", {"start": v(32.53, -12.95) * mm, "end": v(25.53, -12.95) * mm});
            skLineSegment(sketch, "E267.MirrorCS", {"start": v(32.53, 47.05) * mm, "end": v(25.53, 47.05) * mm});
            skLineSegment(sketch, "E268.MirrorCS", {"start": v(40.37, 47.05) * mm, "end": v(33.37, 47.05) * mm});
            skLineSegment(sketch, "E269.MirrorCS", {"start": v(40.37, -48.95) * mm, "end": v(33.37, -48.95) * mm});
            skLineSegment(sketch, "E270.MirrorCS", {"start": v(32.53, -4.95) * mm, "end": v(25.53, -4.95) * mm});
            skLineSegment(sketch, "E271.MirrorCS", {"start": v(48.21, -36.95) * mm, "end": v(41.21, -36.95) * mm});
            skLineSegment(sketch, "E272.MirrorCS", {"start": v(48.21, 3.05) * mm, "end": v(41.21, 3.05) * mm});
            skLineSegment(sketch, "E273.MirrorCS", {"start": v(40.37, 5.05) * mm, "end": v(33.37, 5.05) * mm});
            skLineSegment(sketch, "E274.MirrorCS", {"start": v(32.53, 43.05) * mm, "end": v(25.53, 43.05) * mm});
            skLineSegment(sketch, "E275.MirrorCS", {"start": v(32.53, -28.95) * mm, "end": v(25.53, -28.95) * mm});
            skLineSegment(sketch, "E276.MirrorCS", {"start": v(32.53, 9.05) * mm, "end": v(25.53, 9.05) * mm});
            skLineSegment(sketch, "E277.MirrorCS", {"start": v(40.37, -32.95) * mm, "end": v(33.37, -32.95) * mm});
            skLineSegment(sketch, "E278.MirrorCS", {"start": v(32.53, 39.05) * mm, "end": v(25.53, 39.05) * mm});
            skLineSegment(sketch, "E279.MirrorCS", {"start": v(40.37, 43.05) * mm, "end": v(33.37, 43.05) * mm});
            skLineSegment(sketch, "E280.MirrorCS", {"start": v(40.37, 57.05) * mm, "end": v(33.37, 57.05) * mm});
            skLineSegment(sketch, "E281.MirrorCS", {"start": v(48.21, -34.95) * mm, "end": v(41.21, -34.95) * mm});
            skLineSegment(sketch, "E282.MirrorCS", {"start": v(32.53, -56.95) * mm, "end": v(25.53, -56.95) * mm});
            skLineSegment(sketch, "E283.MirrorCS", {"start": v(48.21, -44.95) * mm, "end": v(41.21, -44.95) * mm});
            skLineSegment(sketch, "E284.MirrorCS", {"start": v(48.21, 43.05) * mm, "end": v(41.21, 43.05) * mm});
            skLineSegment(sketch, "E285.MirrorCS", {"start": v(40.37, 39.05) * mm, "end": v(33.37, 39.05) * mm});
            skLineSegment(sketch, "E286.MirrorCS", {"start": v(32.53, 49.05) * mm, "end": v(25.53, 49.05) * mm});
            skLineSegment(sketch, "E287.MirrorCS", {"start": v(32.53, -20.95) * mm, "end": v(25.53, -20.95) * mm});
            skLineSegment(sketch, "E288.MirrorCS", {"start": v(48.21, 17.05) * mm, "end": v(41.21, 17.05) * mm});
            skLineSegment(sketch, "E289.MirrorCS", {"start": v(40.37, -50.95) * mm, "end": v(33.37, -50.95) * mm});
            skLineSegment(sketch, "E290.MirrorCS", {"start": v(32.53, 23.05) * mm, "end": v(25.53, 23.05) * mm});
            skLineSegment(sketch, "E291.MirrorCS", {"start": v(40.37, 3.05) * mm, "end": v(33.37, 3.05) * mm});
            skLineSegment(sketch, "E292.MirrorCS", {"start": v(32.53, 35.05) * mm, "end": v(25.53, 35.05) * mm});
            skLineSegment(sketch, "E293.MirrorCS", {"start": v(32.53, -8.95) * mm, "end": v(25.53, -8.95) * mm});
            skLineSegment(sketch, "E294.MirrorCS", {"start": v(48.21, -0.95) * mm, "end": v(41.21, -0.95) * mm});
            skLineSegment(sketch, "E295.MirrorCS", {"start": v(48.21, -52.95) * mm, "end": v(41.21, -52.95) * mm});
            skLineSegment(sketch, "E296.MirrorCS", {"start": v(32.53, -38.95) * mm, "end": v(25.53, -38.95) * mm});
            skLineSegment(sketch, "E297.MirrorCS", {"start": v(32.53, -42.95) * mm, "end": v(25.53, -42.95) * mm});
            skLineSegment(sketch, "E298.MirrorCS", {"start": v(32.53, 19.05) * mm, "end": v(25.53, 19.05) * mm});
            skLineSegment(sketch, "E299.MirrorCS", {"start": v(40.37, -34.95) * mm, "end": v(33.37, -34.95) * mm});
            skLineSegment(sketch, "E300.MirrorCS", {"start": v(48.21, 11.05) * mm, "end": v(41.21, 11.05) * mm});
            skLineSegment(sketch, "E301.MirrorCS", {"start": v(48.21, -12.95) * mm, "end": v(41.21, -12.95) * mm});
            skLineSegment(sketch, "E302.MirrorCS", {"start": v(40.37, -52.95) * mm, "end": v(33.37, -52.95) * mm});
            skLineSegment(sketch, "E303.MirrorCS", {"start": v(40.37, 11.05) * mm, "end": v(33.37, 11.05) * mm});
            skLineSegment(sketch, "E304.MirrorCS", {"start": v(48.21, -14.95) * mm, "end": v(41.21, -14.95) * mm});
            skLineSegment(sketch, "E305.MirrorCS", {"start": v(48.21, 25.05) * mm, "end": v(41.21, 25.05) * mm});
            skLineSegment(sketch, "E306.MirrorCS", {"start": v(32.53, -2.95) * mm, "end": v(25.53, -2.95) * mm});
            skLineSegment(sketch, "E307.MirrorCS", {"start": v(48.21, 57.05) * mm, "end": v(41.21, 57.05) * mm});
            skLineSegment(sketch, "E308.MirrorCS", {"start": v(40.37, -36.95) * mm, "end": v(33.37, -36.95) * mm});
            skLineSegment(sketch, "E309.MirrorCS", {"start": v(40.37, -26.95) * mm, "end": v(33.37, -26.95) * mm});
            skLineSegment(sketch, "E310.MirrorCS", {"start": v(32.53, 27.05) * mm, "end": v(25.53, 27.05) * mm});
            skLineSegment(sketch, "E311.MirrorCS", {"start": v(48.21, 49.05) * mm, "end": v(41.21, 49.05) * mm});
            skLineSegment(sketch, "E312.MirrorCS", {"start": v(40.37, -46.95) * mm, "end": v(33.37, -46.95) * mm});
            skLineSegment(sketch, "E313.MirrorCS", {"start": v(40.37, 53.05) * mm, "end": v(33.37, 53.05) * mm});
            skLineSegment(sketch, "E314.MirrorCS", {"start": v(48.21, -10.95) * mm, "end": v(41.21, -10.95) * mm});
            skLineSegment(sketch, "E315.MirrorCS", {"start": v(32.53, -52.95) * mm, "end": v(25.53, -52.95) * mm});
            skLineSegment(sketch, "E316.MirrorCS", {"start": v(32.53, -6.95) * mm, "end": v(25.53, -6.95) * mm});
            skLineSegment(sketch, "E317.MirrorCS", {"start": v(40.37, -44.95) * mm, "end": v(33.37, -44.95) * mm});
            skLineSegment(sketch, "E318.MirrorCS", {"start": v(40.37, -14.95) * mm, "end": v(33.37, -14.95) * mm});
            skLineSegment(sketch, "E319.MirrorCS", {"start": v(32.53, 15.05) * mm, "end": v(25.53, 15.05) * mm});
            skLineSegment(sketch, "E320.MirrorCS", {"start": v(40.37, 29.05) * mm, "end": v(33.37, 29.05) * mm});
            skLineSegment(sketch, "E321.MirrorCS", {"start": v(40.37, -2.95) * mm, "end": v(33.37, -2.95) * mm});
            skLineSegment(sketch, "E322.MirrorCS", {"start": v(48.21, 13.05) * mm, "end": v(41.21, 13.05) * mm});
            skLineSegment(sketch, "E323.MirrorCS", {"start": v(32.53, 37.05) * mm, "end": v(25.53, 37.05) * mm});
            skLineSegment(sketch, "E324.MirrorCS", {"start": v(48.21, -32.95) * mm, "end": v(41.21, -32.95) * mm});
            skLineSegment(sketch, "E325.MirrorCS", {"start": v(40.37, -42.95) * mm, "end": v(33.37, -42.95) * mm});
            skLineSegment(sketch, "E326.MirrorCS", {"start": v(40.37, 37.05) * mm, "end": v(33.37, 37.05) * mm});
            skLineSegment(sketch, "E327.MirrorCS", {"start": v(40.37, -20.95) * mm, "end": v(33.37, -20.95) * mm});
            skLineSegment(sketch, "E328.MirrorCS", {"start": v(32.53, -48.95) * mm, "end": v(25.53, -48.95) * mm});
            skLineSegment(sketch, "E329.MirrorCS", {"start": v(32.53, -54.95) * mm, "end": v(25.53, -54.95) * mm});
            skLineSegment(sketch, "E330.MirrorCS", {"start": v(32.53, 57.05) * mm, "end": v(25.53, 57.05) * mm});
            skLineSegment(sketch, "E331.MirrorCS", {"start": v(32.53, 29.05) * mm, "end": v(25.53, 29.05) * mm});
            skLineSegment(sketch, "E332.MirrorCS", {"start": v(40.37, 21.05) * mm, "end": v(33.37, 21.05) * mm});
            skLineSegment(sketch, "E333.MirrorCS", {"start": v(48.21, 41.05) * mm, "end": v(41.21, 41.05) * mm});
            skLineSegment(sketch, "E334.MirrorCS", {"start": v(48.21, 31.05) * mm, "end": v(41.21, 31.05) * mm});
            skLineSegment(sketch, "E335.MirrorCS", {"start": v(48.21, -30.95) * mm, "end": v(41.21, -30.95) * mm});
            skLineSegment(sketch, "E336.MirrorCS", {"start": v(40.37, 17.05) * mm, "end": v(33.37, 17.05) * mm});
            skLineSegment(sketch, "E337.MirrorCS", {"start": v(48.21, 27.05) * mm, "end": v(41.21, 27.05) * mm});
            skLineSegment(sketch, "E338.MirrorCS", {"start": v(32.53, -0.95) * mm, "end": v(25.53, -0.95) * mm});
            skLineSegment(sketch, "E339.MirrorCS", {"start": v(48.21, -56.95) * mm, "end": v(41.21, -56.95) * mm});
            skLineSegment(sketch, "E340.MirrorCS", {"start": v(32.53, -46.95) * mm, "end": v(25.53, -46.95) * mm});
            skLineSegment(sketch, "E341.MirrorCS", {"start": v(32.53, 5.05) * mm, "end": v(25.53, 5.05) * mm});
            skLineSegment(sketch, "E342.MirrorCS", {"start": v(40.37, -8.95) * mm, "end": v(33.37, -8.95) * mm});
            skLineSegment(sketch, "E343.MirrorCS", {"start": v(48.21, -48.95) * mm, "end": v(41.21, -48.95) * mm});
            skLineSegment(sketch, "E344.MirrorCS", {"start": v(32.53, -24.95) * mm, "end": v(25.53, -24.95) * mm});
            skLineSegment(sketch, "E345.MirrorCS", {"start": v(40.37, 13.05) * mm, "end": v(33.37, 13.05) * mm});
            skLineSegment(sketch, "E346.MirrorCS", {"start": v(48.21, -26.95) * mm, "end": v(41.21, -26.95) * mm});
            skLineSegment(sketch, "E347.MirrorCS", {"start": v(48.21, 37.05) * mm, "end": v(41.21, 37.05) * mm});
            skLineSegment(sketch, "E348.MirrorCS", {"start": v(48.21, -8.95) * mm, "end": v(41.21, -8.95) * mm});
            skLineSegment(sketch, "E349.MirrorCS", {"start": v(32.53, -26.95) * mm, "end": v(25.53, -26.95) * mm});
            skLineSegment(sketch, "E350.MirrorCS", {"start": v(48.21, -38.95) * mm, "end": v(41.21, -38.95) * mm});
            skLineSegment(sketch, "E351.MirrorCS", {"start": v(48.21, 33.05) * mm, "end": v(41.21, 33.05) * mm});
            skLineSegment(sketch, "E352.MirrorCS", {"start": v(40.37, 35.05) * mm, "end": v(33.37, 35.05) * mm});
            skLineSegment(sketch, "E353.MirrorCS", {"start": v(32.53, -36.95) * mm, "end": v(25.53, -36.95) * mm});
            skLineSegment(sketch, "E354.MirrorCS", {"start": v(40.37, -38.95) * mm, "end": v(33.37, -38.95) * mm});
            skLineSegment(sketch, "E355.MirrorCS", {"start": v(32.53, 11.05) * mm, "end": v(25.53, 11.05) * mm});
            skLineSegment(sketch, "E356.MirrorCS", {"start": v(40.37, 41.05) * mm, "end": v(33.37, 41.05) * mm});
            skLineSegment(sketch, "E357.MirrorCS", {"start": v(40.37, 7.05) * mm, "end": v(33.37, 7.05) * mm});
            skLineSegment(sketch, "E358.MirrorCS", {"start": v(40.37, -56.95) * mm, "end": v(33.37, -56.95) * mm});
            skLineSegment(sketch, "E359.MirrorCS", {"start": v(40.37, 31.05) * mm, "end": v(33.37, 31.05) * mm});
            skLineSegment(sketch, "E360.MirrorCS", {"start": v(32.53, -50.95) * mm, "end": v(25.53, -50.95) * mm});
            skLineSegment(sketch, "E361.MirrorCS", {"start": v(48.21, 5.05) * mm, "end": v(41.21, 5.05) * mm});
            skLineSegment(sketch, "E362.MirrorCS", {"start": v(40.37, -18.95) * mm, "end": v(33.37, -18.95) * mm});
            skLineSegment(sketch, "E363.MirrorCS", {"start": v(48.21, 35.05) * mm, "end": v(41.21, 35.05) * mm});
            skLineSegment(sketch, "E364.MirrorCS", {"start": v(40.37, 51.05) * mm, "end": v(33.37, 51.05) * mm});
            skLineSegment(sketch, "E365.MirrorCS", {"start": v(32.53, 51.05) * mm, "end": v(25.53, 51.05) * mm});
            skLineSegment(sketch, "E366.MirrorCS", {"start": v(40.37, 27.05) * mm, "end": v(33.37, 27.05) * mm});
            skLineSegment(sketch, "E367.MirrorCS", {"start": v(48.21, 15.05) * mm, "end": v(41.21, 15.05) * mm});
            skLineSegment(sketch, "E368.MirrorCS", {"start": v(48.21, 21.05) * mm, "end": v(41.21, 21.05) * mm});
            skLineSegment(sketch, "E369.MirrorCS", {"start": v(48.21, 9.05) * mm, "end": v(41.21, 9.05) * mm});
            skLineSegment(sketch, "E370.MirrorCS", {"start": v(32.53, 13.05) * mm, "end": v(25.53, 13.05) * mm});
            skLineSegment(sketch, "E371.MirrorCS", {"start": v(40.37, -28.95) * mm, "end": v(33.37, -28.95) * mm});
            skLineSegment(sketch, "E372.MirrorCS", {"start": v(32.53, 1.05) * mm, "end": v(25.53, 1.05) * mm});
            skLineSegment(sketch, "E373.MirrorCS", {"start": v(48.21, -4.95) * mm, "end": v(41.21, -4.95) * mm});
            skLineSegment(sketch, "E374.MirrorCS", {"start": v(32.53, 21.05) * mm, "end": v(25.53, 21.05) * mm});
            skLineSegment(sketch, "E375.MirrorCS", {"start": v(40.37, 9.05) * mm, "end": v(33.37, 9.05) * mm});
            skLineSegment(sketch, "E376.MirrorCS", {"start": v(40.37, -40.95) * mm, "end": v(33.37, -40.95) * mm});
            skLineSegment(sketch, "E377.MirrorCS", {"start": v(48.21, 1.05) * mm, "end": v(41.21, 1.05) * mm});
            skLineSegment(sketch, "E378.MirrorCS", {"start": v(40.37, 1.05) * mm, "end": v(33.37, 1.05) * mm});
            skLineSegment(sketch, "E379.MirrorCS", {"start": v(48.21, 55.05) * mm, "end": v(41.21, 55.05) * mm});
            skLineSegment(sketch, "E380.MirrorCS", {"start": v(32.53, -30.95) * mm, "end": v(25.53, -30.95) * mm});
            skLineSegment(sketch, "E381.MirrorCS", {"start": v(32.53, -10.95) * mm, "end": v(25.53, -10.95) * mm});
            skLineSegment(sketch, "E382.MirrorCS", {"start": v(32.53, 41.05) * mm, "end": v(25.53, 41.05) * mm});
            skLineSegment(sketch, "E383.MirrorCS", {"start": v(32.53, 53.05) * mm, "end": v(25.53, 53.05) * mm});
            skLineSegment(sketch, "E384.MirrorCS", {"start": v(40.37, 25.05) * mm, "end": v(33.37, 25.05) * mm});
            skLineSegment(sketch, "E385.MirrorCS", {"start": v(40.37, -24.95) * mm, "end": v(33.37, -24.95) * mm});
            skLineSegment(sketch, "E386.MirrorCS", {"start": v(48.21, 19.05) * mm, "end": v(41.21, 19.05) * mm});
            skLineSegment(sketch, "E387.MirrorCS", {"start": v(40.37, -16.95) * mm, "end": v(33.37, -16.95) * mm});
            skLineSegment(sketch, "E388.MirrorCS", {"start": v(32.53, 7.05) * mm, "end": v(25.53, 7.05) * mm});
            skLineSegment(sketch, "E389.MirrorCS", {"start": v(48.21, -16.95) * mm, "end": v(41.21, -16.95) * mm});
            skSolve(sketch);
        }
        {
            var Q0;
            Q0 = qSketchRegion(id + "F7", true);
            extrude(context, id + "F8", {"entities" : qUnion([Q0]), "operationType" : NewBodyOperationType.REMOVE, "oppositeDirection" : true, "depth" : 25 * mm, "offsetDistance" : 25 * mm});
        }
    });
